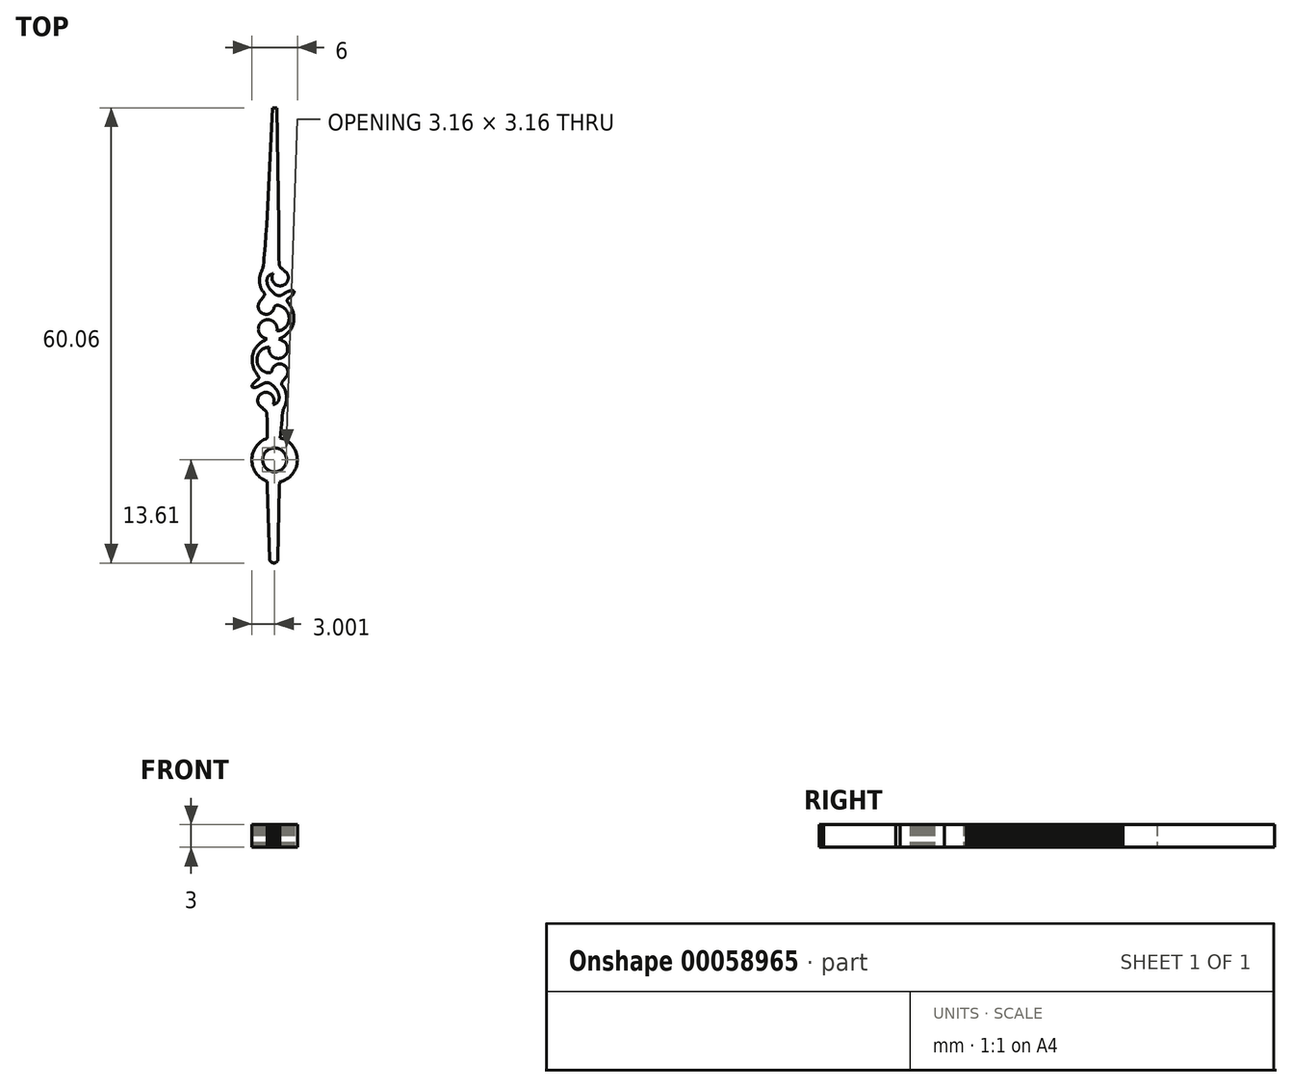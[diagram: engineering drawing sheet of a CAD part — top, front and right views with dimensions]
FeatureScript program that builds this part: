
annotation { "Feature Type Name" : "Feature", "Feature Type Description" : "" }
export const myFeature = defineFeature(function(context is Context, id is Id, definition is map)
    precondition{}
    {
        {
            var Q0;
            Q0=qCreatedBy(makeId("Top.planeOp"),FACE);
            var sketch = newSketch(context, id + "F0", { "sketchPlane" : qUnion([Q0])});
            skLineSegment(sketch, "E0", {"start": v(-0.15, 30.03) * mm, "end": v(0.45, 30.03) * mm});
            skLineSegment(sketch, "E1", {"start": v(0.45, 30.03) * mm, "end": v(0.66, 14.62) * mm});
            skLineSegment(sketch, "E2", {"start": v(0.66, 14.62) * mm, "end": v(0.66, 13.4) * mm});
            skLineSegment(sketch, "E3", {"start": v(0.66, 13.4) * mm, "end": v(0.67, 12.16) * mm});
            skLineSegment(sketch, "E4", {"start": v(0.67, 12.16) * mm, "end": v(0.68, 11.56) * mm});
            skLineSegment(sketch, "E5", {"start": v(0.68, 11.56) * mm, "end": v(0.69, 11) * mm});
            skLineSegment(sketch, "E6", {"start": v(0.69, 11) * mm, "end": v(0.7, 10.49) * mm});
            skLineSegment(sketch, "E7", {"start": v(0.7, 10.49) * mm, "end": v(0.72, 10.03) * mm});
            skLineSegment(sketch, "E8", {"start": v(0.72, 10.03) * mm, "end": v(0.73, 9.66) * mm});
            skLineSegment(sketch, "E9", {"start": v(0.73, 9.66) * mm, "end": v(0.75, 9.37) * mm});
            skLineSegment(sketch, "E10", {"start": v(0.75, 9.37) * mm, "end": v(0.76, 9.3) * mm});
            skLineSegment(sketch, "E11", {"start": v(0.76, 9.3) * mm, "end": v(0.78, 9.23) * mm});
            skLineSegment(sketch, "E12", {"start": v(0.78, 9.23) * mm, "end": v(0.8, 9.16) * mm});
            skLineSegment(sketch, "E13", {"start": v(0.8, 9.16) * mm, "end": v(0.83, 9.1) * mm});
            skLineSegment(sketch, "E14", {"start": v(0.83, 9.1) * mm, "end": v(0.87, 9.05) * mm});
            skLineSegment(sketch, "E15", {"start": v(0.87, 9.05) * mm, "end": v(0.9, 9) * mm});
            skLineSegment(sketch, "E16", {"start": v(0.9, 9) * mm, "end": v(0.94, 8.95) * mm});
            skLineSegment(sketch, "E17", {"start": v(0.94, 8.95) * mm, "end": v(0.98, 8.91) * mm});
            skLineSegment(sketch, "E18", {"start": v(0.98, 8.91) * mm, "end": v(1.07, 8.83) * mm});
            skLineSegment(sketch, "E19", {"start": v(1.07, 8.83) * mm, "end": v(1.16, 8.76) * mm});
            skLineSegment(sketch, "E20", {"start": v(1.16, 8.76) * mm, "end": v(1.25, 8.68) * mm});
            skLineSegment(sketch, "E21", {"start": v(1.25, 8.68) * mm, "end": v(1.29, 8.64) * mm});
            skLineSegment(sketch, "E22", {"start": v(1.29, 8.64) * mm, "end": v(1.32, 8.6) * mm});
            skLineSegment(sketch, "E23", {"start": v(1.32, 8.6) * mm, "end": v(1.32, 8.6) * mm});
            skLineSegment(sketch, "E24", {"start": v(1.32, 8.6) * mm, "end": v(1.46, 8.5) * mm});
            skLineSegment(sketch, "E25", {"start": v(1.46, 8.5) * mm, "end": v(1.52, 8.44) * mm});
            skLineSegment(sketch, "E26", {"start": v(1.52, 8.44) * mm, "end": v(1.58, 8.4) * mm});
            skLineSegment(sketch, "E27", {"start": v(1.58, 8.4) * mm, "end": v(1.64, 8.34) * mm});
            skLineSegment(sketch, "E28", {"start": v(1.64, 8.34) * mm, "end": v(1.69, 8.28) * mm});
            skLineSegment(sketch, "E29", {"start": v(1.69, 8.28) * mm, "end": v(1.74, 8.23) * mm});
            skLineSegment(sketch, "E30", {"start": v(1.74, 8.23) * mm, "end": v(1.78, 8.17) * mm});
            skLineSegment(sketch, "E31", {"start": v(1.78, 8.17) * mm, "end": v(1.82, 8.11) * mm});
            skLineSegment(sketch, "E32", {"start": v(1.82, 8.11) * mm, "end": v(1.85, 8.05) * mm});
            skLineSegment(sketch, "E33", {"start": v(1.85, 8.05) * mm, "end": v(1.88, 7.99) * mm});
            skLineSegment(sketch, "E34", {"start": v(1.88, 7.99) * mm, "end": v(1.9, 7.92) * mm});
            skLineSegment(sketch, "E35", {"start": v(1.9, 7.92) * mm, "end": v(1.92, 7.85) * mm});
            skLineSegment(sketch, "E36", {"start": v(1.92, 7.85) * mm, "end": v(1.94, 7.78) * mm});
            skLineSegment(sketch, "E37", {"start": v(1.94, 7.78) * mm, "end": v(1.94, 7.7) * mm});
            skLineSegment(sketch, "E38", {"start": v(1.94, 7.7) * mm, "end": v(1.95, 7.62) * mm});
            skLineSegment(sketch, "E39", {"start": v(1.95, 7.62) * mm, "end": v(1.94, 7.57) * mm});
            skLineSegment(sketch, "E40", {"start": v(1.94, 7.57) * mm, "end": v(1.94, 7.51) * mm});
            skLineSegment(sketch, "E41", {"start": v(1.94, 7.51) * mm, "end": v(1.93, 7.46) * mm});
            skLineSegment(sketch, "E42", {"start": v(1.93, 7.46) * mm, "end": v(1.92, 7.4) * mm});
            skLineSegment(sketch, "E43", {"start": v(1.92, 7.4) * mm, "end": v(1.91, 7.35) * mm});
            skLineSegment(sketch, "E44", {"start": v(1.91, 7.35) * mm, "end": v(1.9, 7.3) * mm});
            skLineSegment(sketch, "E45", {"start": v(1.9, 7.3) * mm, "end": v(1.88, 7.25) * mm});
            skLineSegment(sketch, "E46", {"start": v(1.88, 7.25) * mm, "end": v(1.86, 7.2) * mm});
            skLineSegment(sketch, "E47", {"start": v(1.86, 7.2) * mm, "end": v(1.84, 7.16) * mm});
            skLineSegment(sketch, "E48", {"start": v(1.84, 7.16) * mm, "end": v(1.82, 7.1) * mm});
            skLineSegment(sketch, "E49", {"start": v(1.82, 7.1) * mm, "end": v(1.76, 7.02) * mm});
            skLineSegment(sketch, "E50", {"start": v(1.76, 7.02) * mm, "end": v(1.7, 6.94) * mm});
            skLineSegment(sketch, "E51", {"start": v(1.7, 6.94) * mm, "end": v(1.63, 6.86) * mm});
            skLineSegment(sketch, "E52", {"start": v(1.63, 6.86) * mm, "end": v(1.55, 6.79) * mm});
            skLineSegment(sketch, "E53", {"start": v(1.55, 6.79) * mm, "end": v(1.47, 6.73) * mm});
            skLineSegment(sketch, "E54", {"start": v(1.47, 6.73) * mm, "end": v(1.38, 6.67) * mm});
            skLineSegment(sketch, "E55", {"start": v(1.38, 6.67) * mm, "end": v(1.33, 6.65) * mm});
            skLineSegment(sketch, "E56", {"start": v(1.33, 6.65) * mm, "end": v(1.29, 6.63) * mm});
            skLineSegment(sketch, "E57", {"start": v(1.29, 6.63) * mm, "end": v(1.24, 6.6) * mm});
            skLineSegment(sketch, "E58", {"start": v(1.24, 6.6) * mm, "end": v(1.19, 6.6) * mm});
            skLineSegment(sketch, "E59", {"start": v(1.19, 6.6) * mm, "end": v(1.13, 6.58) * mm});
            skLineSegment(sketch, "E60", {"start": v(1.13, 6.58) * mm, "end": v(1.08, 6.56) * mm});
            skLineSegment(sketch, "E61", {"start": v(1.08, 6.56) * mm, "end": v(1.03, 6.56) * mm});
            skLineSegment(sketch, "E62", {"start": v(1.03, 6.56) * mm, "end": v(0.97, 6.55) * mm});
            skLineSegment(sketch, "E63", {"start": v(0.97, 6.55) * mm, "end": v(0.92, 6.54) * mm});
            skLineSegment(sketch, "E64", {"start": v(0.92, 6.54) * mm, "end": v(0.86, 6.54) * mm});
            skLineSegment(sketch, "E65", {"start": v(0.86, 6.54) * mm, "end": v(0.8, 6.54) * mm});
            skLineSegment(sketch, "E66", {"start": v(0.8, 6.54) * mm, "end": v(0.75, 6.55) * mm});
            skLineSegment(sketch, "E67", {"start": v(0.75, 6.55) * mm, "end": v(0.7, 6.56) * mm});
            skLineSegment(sketch, "E68", {"start": v(0.7, 6.56) * mm, "end": v(0.65, 6.56) * mm});
            skLineSegment(sketch, "E69", {"start": v(0.65, 6.56) * mm, "end": v(0.6, 6.58) * mm});
            skLineSegment(sketch, "E70", {"start": v(0.6, 6.58) * mm, "end": v(0.54, 6.6) * mm});
            skLineSegment(sketch, "E71", {"start": v(0.54, 6.6) * mm, "end": v(0.5, 6.6) * mm});
            skLineSegment(sketch, "E72", {"start": v(0.5, 6.6) * mm, "end": v(0.44, 6.63) * mm});
            skLineSegment(sketch, "E73", {"start": v(0.44, 6.63) * mm, "end": v(0.4, 6.65) * mm});
            skLineSegment(sketch, "E74", {"start": v(0.4, 6.65) * mm, "end": v(0.35, 6.67) * mm});
            skLineSegment(sketch, "E75", {"start": v(0.35, 6.67) * mm, "end": v(0.26, 6.73) * mm});
            skLineSegment(sketch, "E76", {"start": v(0.26, 6.73) * mm, "end": v(0.18, 6.79) * mm});
            skLineSegment(sketch, "E77", {"start": v(0.18, 6.79) * mm, "end": v(0.1, 6.86) * mm});
            skLineSegment(sketch, "E78", {"start": v(0.1, 6.86) * mm, "end": v(0.03, 6.94) * mm});
            skLineSegment(sketch, "E79", {"start": v(0.03, 6.94) * mm, "end": v(-0.03, 7.02) * mm});
            skLineSegment(sketch, "E80", {"start": v(-0.03, 7.02) * mm, "end": v(-0.09, 7.1) * mm});
            skLineSegment(sketch, "E81", {"start": v(-0.09, 7.1) * mm, "end": v(-0.11, 7.16) * mm});
            skLineSegment(sketch, "E82", {"start": v(-0.11, 7.16) * mm, "end": v(-0.13, 7.2) * mm});
            skLineSegment(sketch, "E83", {"start": v(-0.13, 7.2) * mm, "end": v(-0.15, 7.25) * mm});
            skLineSegment(sketch, "E84", {"start": v(-0.15, 7.25) * mm, "end": v(-0.17, 7.3) * mm});
            skLineSegment(sketch, "E85", {"start": v(-0.17, 7.3) * mm, "end": v(-0.18, 7.35) * mm});
            skLineSegment(sketch, "E86", {"start": v(-0.18, 7.35) * mm, "end": v(-0.2, 7.4) * mm});
            skLineSegment(sketch, "E87", {"start": v(-0.2, 7.4) * mm, "end": v(-0.2, 7.46) * mm});
            skLineSegment(sketch, "E88", {"start": v(-0.2, 7.46) * mm, "end": v(-0.21, 7.51) * mm});
            skLineSegment(sketch, "E89", {"start": v(-0.21, 7.51) * mm, "end": v(-0.22, 7.57) * mm});
            skLineSegment(sketch, "E90", {"start": v(-0.22, 7.57) * mm, "end": v(-0.22, 7.62) * mm});
            skLineSegment(sketch, "E91", {"start": v(-0.22, 7.62) * mm, "end": v(-0.22, 7.7) * mm});
            skLineSegment(sketch, "E92", {"start": v(-0.22, 7.7) * mm, "end": v(-0.2, 7.77) * mm});
            skLineSegment(sketch, "E93", {"start": v(-0.2, 7.77) * mm, "end": v(-0.2, 7.84) * mm});
            skLineSegment(sketch, "E94", {"start": v(-0.2, 7.84) * mm, "end": v(-0.18, 7.9) * mm});
            skLineSegment(sketch, "E95", {"start": v(-0.18, 7.9) * mm, "end": v(-0.16, 7.97) * mm});
            skLineSegment(sketch, "E96", {"start": v(-0.16, 7.97) * mm, "end": v(-0.14, 8.04) * mm});
            skLineSegment(sketch, "E97", {"start": v(-0.14, 8.04) * mm, "end": v(-0.1, 8.1) * mm});
            skLineSegment(sketch, "E98", {"start": v(-0.1, 8.1) * mm, "end": v(-0.08, 8.16) * mm});
            skLineSegment(sketch, "E99", {"start": v(-0.08, 8.16) * mm, "end": v(-0.1, 8.16) * mm});
            skLineSegment(sketch, "E100", {"start": v(-0.1, 8.16) * mm, "end": v(-0.14, 8.15) * mm});
            skLineSegment(sketch, "E101", {"start": v(-0.14, 8.15) * mm, "end": v(-0.23, 8.11) * mm});
            skLineSegment(sketch, "E102", {"start": v(-0.23, 8.11) * mm, "end": v(-0.34, 8.06) * mm});
            skLineSegment(sketch, "E103", {"start": v(-0.34, 8.06) * mm, "end": v(-0.48, 8) * mm});
            skLineSegment(sketch, "E104", {"start": v(-0.48, 8) * mm, "end": v(-0.53, 7.97) * mm});
            skLineSegment(sketch, "E105", {"start": v(-0.53, 7.97) * mm, "end": v(-0.58, 7.94) * mm});
            skLineSegment(sketch, "E106", {"start": v(-0.58, 7.94) * mm, "end": v(-0.62, 7.9) * mm});
            skLineSegment(sketch, "E107", {"start": v(-0.62, 7.9) * mm, "end": v(-0.66, 7.86) * mm});
            skLineSegment(sketch, "E108", {"start": v(-0.66, 7.86) * mm, "end": v(-0.7, 7.82) * mm});
            skLineSegment(sketch, "E109", {"start": v(-0.7, 7.82) * mm, "end": v(-0.74, 7.77) * mm});
            skLineSegment(sketch, "E110", {"start": v(-0.74, 7.77) * mm, "end": v(-0.77, 7.72) * mm});
            skLineSegment(sketch, "E111", {"start": v(-0.77, 7.72) * mm, "end": v(-0.8, 7.67) * mm});
            skLineSegment(sketch, "E112", {"start": v(-0.8, 7.67) * mm, "end": v(-0.82, 7.62) * mm});
            skLineSegment(sketch, "E113", {"start": v(-0.82, 7.62) * mm, "end": v(-0.84, 7.56) * mm});
            skLineSegment(sketch, "E114", {"start": v(-0.84, 7.56) * mm, "end": v(-0.85, 7.5) * mm});
            skLineSegment(sketch, "E115", {"start": v(-0.85, 7.5) * mm, "end": v(-0.87, 7.44) * mm});
            skLineSegment(sketch, "E116", {"start": v(-0.87, 7.44) * mm, "end": v(-0.88, 7.38) * mm});
            skLineSegment(sketch, "E117", {"start": v(-0.88, 7.38) * mm, "end": v(-0.88, 7.31) * mm});
            skLineSegment(sketch, "E118", {"start": v(-0.88, 7.31) * mm, "end": v(-0.88, 7.25) * mm});
            skLineSegment(sketch, "E119", {"start": v(-0.88, 7.25) * mm, "end": v(-0.88, 7.18) * mm});
            skLineSegment(sketch, "E120", {"start": v(-0.88, 7.18) * mm, "end": v(-0.88, 7.1) * mm});
            skLineSegment(sketch, "E121", {"start": v(-0.88, 7.1) * mm, "end": v(-0.87, 7.04) * mm});
            skLineSegment(sketch, "E122", {"start": v(-0.87, 7.04) * mm, "end": v(-0.86, 6.97) * mm});
            skLineSegment(sketch, "E123", {"start": v(-0.86, 6.97) * mm, "end": v(-0.84, 6.9) * mm});
            skLineSegment(sketch, "E124", {"start": v(-0.84, 6.9) * mm, "end": v(-0.83, 6.82) * mm});
            skLineSegment(sketch, "E125", {"start": v(-0.83, 6.82) * mm, "end": v(-0.8, 6.75) * mm});
            skLineSegment(sketch, "E126", {"start": v(-0.8, 6.75) * mm, "end": v(-0.78, 6.68) * mm});
            skLineSegment(sketch, "E127", {"start": v(-0.78, 6.68) * mm, "end": v(-0.75, 6.6) * mm});
            skLineSegment(sketch, "E128", {"start": v(-0.75, 6.6) * mm, "end": v(-0.72, 6.53) * mm});
            skLineSegment(sketch, "E129", {"start": v(-0.72, 6.53) * mm, "end": v(-0.68, 6.45) * mm});
            skLineSegment(sketch, "E130", {"start": v(-0.68, 6.45) * mm, "end": v(-0.64, 6.38) * mm});
            skLineSegment(sketch, "E131", {"start": v(-0.64, 6.38) * mm, "end": v(-0.6, 6.3) * mm});
            skLineSegment(sketch, "E132", {"start": v(-0.6, 6.3) * mm, "end": v(-0.56, 6.23) * mm});
            skLineSegment(sketch, "E133", {"start": v(-0.56, 6.23) * mm, "end": v(-0.5, 6.16) * mm});
            skLineSegment(sketch, "E134", {"start": v(-0.5, 6.16) * mm, "end": v(-0.45, 6.09) * mm});
            skLineSegment(sketch, "E135", {"start": v(-0.45, 6.09) * mm, "end": v(-0.4, 6.02) * mm});
            skLineSegment(sketch, "E136", {"start": v(-0.4, 6.02) * mm, "end": v(-0.27, 5.87) * mm});
            skLineSegment(sketch, "E137", {"start": v(-0.27, 5.87) * mm, "end": v(-0.15, 5.73) * mm});
            skLineSegment(sketch, "E138", {"start": v(-0.15, 5.73) * mm, "end": v(-0.03, 5.62) * mm});
            skLineSegment(sketch, "E139", {"start": v(-0.03, 5.62) * mm, "end": v(0.03, 5.57) * mm});
            skLineSegment(sketch, "E140", {"start": v(0.03, 5.57) * mm, "end": v(0.08, 5.52) * mm});
            skLineSegment(sketch, "E141", {"start": v(0.08, 5.52) * mm, "end": v(0.14, 5.47) * mm});
            skLineSegment(sketch, "E142", {"start": v(0.14, 5.47) * mm, "end": v(0.2, 5.43) * mm});
            skLineSegment(sketch, "E143", {"start": v(0.2, 5.43) * mm, "end": v(0.25, 5.4) * mm});
            skLineSegment(sketch, "E144", {"start": v(0.25, 5.4) * mm, "end": v(0.3, 5.37) * mm});
            skLineSegment(sketch, "E145", {"start": v(0.3, 5.37) * mm, "end": v(0.36, 5.34) * mm});
            skLineSegment(sketch, "E146", {"start": v(0.36, 5.34) * mm, "end": v(0.42, 5.32) * mm});
            skLineSegment(sketch, "E147", {"start": v(0.42, 5.32) * mm, "end": v(0.47, 5.3) * mm});
            skLineSegment(sketch, "E148", {"start": v(0.47, 5.3) * mm, "end": v(0.53, 5.28) * mm});
            skLineSegment(sketch, "E149", {"start": v(0.53, 5.28) * mm, "end": v(0.58, 5.27) * mm});
            skLineSegment(sketch, "E150", {"start": v(0.58, 5.27) * mm, "end": v(0.64, 5.26) * mm});
            skLineSegment(sketch, "E151", {"start": v(0.64, 5.26) * mm, "end": v(0.7, 5.26) * mm});
            skLineSegment(sketch, "E152", {"start": v(0.7, 5.26) * mm, "end": v(0.75, 5.26) * mm});
            skLineSegment(sketch, "E153", {"start": v(0.75, 5.26) * mm, "end": v(0.8, 5.26) * mm});
            skLineSegment(sketch, "E154", {"start": v(0.8, 5.26) * mm, "end": v(0.86, 5.27) * mm});
            skLineSegment(sketch, "E155", {"start": v(0.86, 5.27) * mm, "end": v(0.92, 5.28) * mm});
            skLineSegment(sketch, "E156", {"start": v(0.92, 5.28) * mm, "end": v(0.98, 5.3) * mm});
            skLineSegment(sketch, "E157", {"start": v(0.98, 5.3) * mm, "end": v(1.04, 5.31) * mm});
            skLineSegment(sketch, "E158", {"start": v(1.04, 5.31) * mm, "end": v(1.1, 5.33) * mm});
            skLineSegment(sketch, "E159", {"start": v(1.1, 5.33) * mm, "end": v(1.16, 5.36) * mm});
            skLineSegment(sketch, "E160", {"start": v(1.16, 5.36) * mm, "end": v(1.22, 5.4) * mm});
            skLineSegment(sketch, "E161", {"start": v(1.22, 5.4) * mm, "end": v(1.28, 5.42) * mm});
            skLineSegment(sketch, "E162", {"start": v(1.28, 5.42) * mm, "end": v(1.34, 5.46) * mm});
            skLineSegment(sketch, "E163", {"start": v(1.34, 5.46) * mm, "end": v(1.47, 5.55) * mm});
            skLineSegment(sketch, "E164", {"start": v(1.47, 5.55) * mm, "end": v(1.58, 5.61) * mm});
            skLineSegment(sketch, "E165", {"start": v(1.58, 5.61) * mm, "end": v(1.67, 5.67) * mm});
            skLineSegment(sketch, "E166", {"start": v(1.67, 5.67) * mm, "end": v(1.77, 5.73) * mm});
            skLineSegment(sketch, "E167", {"start": v(1.77, 5.73) * mm, "end": v(1.86, 5.77) * mm});
            skLineSegment(sketch, "E168", {"start": v(1.86, 5.77) * mm, "end": v(1.95, 5.81) * mm});
            skLineSegment(sketch, "E169", {"start": v(1.95, 5.81) * mm, "end": v(2.03, 5.85) * mm});
            skLineSegment(sketch, "E170", {"start": v(2.03, 5.85) * mm, "end": v(2.11, 5.88) * mm});
            skLineSegment(sketch, "E171", {"start": v(2.11, 5.88) * mm, "end": v(2.2, 5.9) * mm});
            skLineSegment(sketch, "E172", {"start": v(2.2, 5.9) * mm, "end": v(2.26, 5.92) * mm});
            skLineSegment(sketch, "E173", {"start": v(2.26, 5.92) * mm, "end": v(2.33, 5.93) * mm});
            skLineSegment(sketch, "E174", {"start": v(2.33, 5.93) * mm, "end": v(2.4, 5.93) * mm});
            skLineSegment(sketch, "E175", {"start": v(2.4, 5.93) * mm, "end": v(2.45, 5.93) * mm});
            skLineSegment(sketch, "E176", {"start": v(2.45, 5.93) * mm, "end": v(2.5, 5.93) * mm});
            skLineSegment(sketch, "E177", {"start": v(2.5, 5.93) * mm, "end": v(2.55, 5.92) * mm});
            skLineSegment(sketch, "E178", {"start": v(2.55, 5.92) * mm, "end": v(2.59, 5.9) * mm});
            skLineSegment(sketch, "E179", {"start": v(2.59, 5.9) * mm, "end": v(2.62, 5.88) * mm});
            skLineSegment(sketch, "E180", {"start": v(2.62, 5.88) * mm, "end": v(2.65, 5.86) * mm});
            skLineSegment(sketch, "E181", {"start": v(2.65, 5.86) * mm, "end": v(2.67, 5.83) * mm});
            skLineSegment(sketch, "E182", {"start": v(2.67, 5.83) * mm, "end": v(2.69, 5.8) * mm});
            skLineSegment(sketch, "E183", {"start": v(2.69, 5.8) * mm, "end": v(2.7, 5.76) * mm});
            skLineSegment(sketch, "E184", {"start": v(2.7, 5.76) * mm, "end": v(2.7, 5.72) * mm});
            skLineSegment(sketch, "E185", {"start": v(2.7, 5.72) * mm, "end": v(2.7, 5.67) * mm});
            skLineSegment(sketch, "E186", {"start": v(2.7, 5.67) * mm, "end": v(2.68, 5.63) * mm});
            skLineSegment(sketch, "E187", {"start": v(2.68, 5.63) * mm, "end": v(2.66, 5.57) * mm});
            skLineSegment(sketch, "E188", {"start": v(2.66, 5.57) * mm, "end": v(2.63, 5.52) * mm});
            skLineSegment(sketch, "E189", {"start": v(2.63, 5.52) * mm, "end": v(2.6, 5.46) * mm});
            skLineSegment(sketch, "E190", {"start": v(2.6, 5.46) * mm, "end": v(2.54, 5.4) * mm});
            skLineSegment(sketch, "E191", {"start": v(2.54, 5.4) * mm, "end": v(2.5, 5.34) * mm});
            skLineSegment(sketch, "E192", {"start": v(2.5, 5.34) * mm, "end": v(2.43, 5.27) * mm});
            skLineSegment(sketch, "E193", {"start": v(2.43, 5.27) * mm, "end": v(2.35, 5.2) * mm});
            skLineSegment(sketch, "E194", {"start": v(2.35, 5.2) * mm, "end": v(2.27, 5.13) * mm});
            skLineSegment(sketch, "E195", {"start": v(2.27, 5.13) * mm, "end": v(2.18, 5.05) * mm});
            skLineSegment(sketch, "E196", {"start": v(2.18, 5.05) * mm, "end": v(2, 4.92) * mm});
            skLineSegment(sketch, "E197", {"start": v(2, 4.92) * mm, "end": v(1.94, 4.86) * mm});
            skLineSegment(sketch, "E198", {"start": v(1.94, 4.86) * mm, "end": v(1.89, 4.81) * mm});
            skLineSegment(sketch, "E199", {"start": v(1.89, 4.81) * mm, "end": v(1.85, 4.76) * mm});
            skLineSegment(sketch, "E200", {"start": v(1.85, 4.76) * mm, "end": v(1.81, 4.71) * mm});
            skLineSegment(sketch, "E201", {"start": v(1.81, 4.71) * mm, "end": v(1.8, 4.69) * mm});
            skLineSegment(sketch, "E202", {"start": v(1.8, 4.69) * mm, "end": v(1.8, 4.67) * mm});
            skLineSegment(sketch, "E203", {"start": v(1.8, 4.67) * mm, "end": v(1.8, 4.64) * mm});
            skLineSegment(sketch, "E204", {"start": v(1.8, 4.64) * mm, "end": v(1.79, 4.62) * mm});
            skLineSegment(sketch, "E205", {"start": v(1.79, 4.62) * mm, "end": v(1.8, 4.59) * mm});
            skLineSegment(sketch, "E206", {"start": v(1.8, 4.59) * mm, "end": v(1.8, 4.56) * mm});
            skLineSegment(sketch, "E207", {"start": v(1.8, 4.56) * mm, "end": v(1.81, 4.5) * mm});
            skLineSegment(sketch, "E208", {"start": v(1.81, 4.5) * mm, "end": v(1.84, 4.44) * mm});
            skLineSegment(sketch, "E209", {"start": v(1.84, 4.44) * mm, "end": v(1.88, 4.36) * mm});
            skLineSegment(sketch, "E210", {"start": v(1.88, 4.36) * mm, "end": v(1.93, 4.28) * mm});
            skLineSegment(sketch, "E211", {"start": v(1.93, 4.28) * mm, "end": v(2, 4.18) * mm});
            skLineSegment(sketch, "E212", {"start": v(2, 4.18) * mm, "end": v(2.16, 3.95) * mm});
            skLineSegment(sketch, "E213", {"start": v(2.16, 3.95) * mm, "end": v(2.23, 3.86) * mm});
            skLineSegment(sketch, "E214", {"start": v(2.23, 3.86) * mm, "end": v(2.29, 3.76) * mm});
            skLineSegment(sketch, "E215", {"start": v(2.29, 3.76) * mm, "end": v(2.34, 3.66) * mm});
            skLineSegment(sketch, "E216", {"start": v(2.34, 3.66) * mm, "end": v(2.4, 3.56) * mm});
            skLineSegment(sketch, "E217", {"start": v(2.4, 3.56) * mm, "end": v(2.44, 3.45) * mm});
            skLineSegment(sketch, "E218", {"start": v(2.44, 3.45) * mm, "end": v(2.49, 3.34) * mm});
            skLineSegment(sketch, "E219", {"start": v(2.49, 3.34) * mm, "end": v(2.53, 3.23) * mm});
            skLineSegment(sketch, "E220", {"start": v(2.53, 3.23) * mm, "end": v(2.56, 3.12) * mm});
            skLineSegment(sketch, "E221", {"start": v(2.56, 3.12) * mm, "end": v(2.59, 3) * mm});
            skLineSegment(sketch, "E222", {"start": v(2.59, 3) * mm, "end": v(2.62, 2.9) * mm});
            skLineSegment(sketch, "E223", {"start": v(2.62, 2.9) * mm, "end": v(2.64, 2.78) * mm});
            skLineSegment(sketch, "E224", {"start": v(2.64, 2.78) * mm, "end": v(2.65, 2.66) * mm});
            skLineSegment(sketch, "E225", {"start": v(2.65, 2.66) * mm, "end": v(2.67, 2.55) * mm});
            skLineSegment(sketch, "E226", {"start": v(2.67, 2.55) * mm, "end": v(2.68, 2.43) * mm});
            skLineSegment(sketch, "E227", {"start": v(2.68, 2.43) * mm, "end": v(2.68, 2.31) * mm});
            skLineSegment(sketch, "E228", {"start": v(2.68, 2.31) * mm, "end": v(2.68, 2.2) * mm});
            skLineSegment(sketch, "E229", {"start": v(2.68, 2.2) * mm, "end": v(2.67, 2.08) * mm});
            skLineSegment(sketch, "E230", {"start": v(2.67, 2.08) * mm, "end": v(2.67, 1.96) * mm});
            skLineSegment(sketch, "E231", {"start": v(2.67, 1.96) * mm, "end": v(2.65, 1.85) * mm});
            skLineSegment(sketch, "E232", {"start": v(2.65, 1.85) * mm, "end": v(2.64, 1.74) * mm});
            skLineSegment(sketch, "E233", {"start": v(2.64, 1.74) * mm, "end": v(2.61, 1.62) * mm});
            skLineSegment(sketch, "E234", {"start": v(2.61, 1.62) * mm, "end": v(2.59, 1.51) * mm});
            skLineSegment(sketch, "E235", {"start": v(2.59, 1.51) * mm, "end": v(2.56, 1.4) * mm});
            skLineSegment(sketch, "E236", {"start": v(2.56, 1.4) * mm, "end": v(2.52, 1.3) * mm});
            skLineSegment(sketch, "E237", {"start": v(2.52, 1.3) * mm, "end": v(2.49, 1.2) * mm});
            skLineSegment(sketch, "E238", {"start": v(2.49, 1.2) * mm, "end": v(2.44, 1.09) * mm});
            skLineSegment(sketch, "E239", {"start": v(2.44, 1.09) * mm, "end": v(2.4, 0.99) * mm});
            skLineSegment(sketch, "E240", {"start": v(2.4, 0.99) * mm, "end": v(2.34, 0.9) * mm});
            skLineSegment(sketch, "E241", {"start": v(2.34, 0.9) * mm, "end": v(2.29, 0.8) * mm});
            skLineSegment(sketch, "E242", {"start": v(2.29, 0.8) * mm, "end": v(2.23, 0.7) * mm});
            skLineSegment(sketch, "E243", {"start": v(2.23, 0.7) * mm, "end": v(2.16, 0.62) * mm});
            skLineSegment(sketch, "E244", {"start": v(2.16, 0.62) * mm, "end": v(2.1, 0.54) * mm});
            skLineSegment(sketch, "E245", {"start": v(2.1, 0.54) * mm, "end": v(1.97, 0.4) * mm});
            skLineSegment(sketch, "E246", {"start": v(1.97, 0.4) * mm, "end": v(1.84, 0.27) * mm});
            skLineSegment(sketch, "E247", {"start": v(1.84, 0.27) * mm, "end": v(1.71, 0.15) * mm});
            skLineSegment(sketch, "E248", {"start": v(1.71, 0.15) * mm, "end": v(1.58, 0.03) * mm});
            skLineSegment(sketch, "E249", {"start": v(1.58, 0.03) * mm, "end": v(1.44, -0.07) * mm});
            skLineSegment(sketch, "E250", {"start": v(1.44, -0.07) * mm, "end": v(1.3, -0.17) * mm});
            skLineSegment(sketch, "E251", {"start": v(1.3, -0.17) * mm, "end": v(1.15, -0.26) * mm});
            skLineSegment(sketch, "E252", {"start": v(1.15, -0.26) * mm, "end": v(1.01, -0.34) * mm});
            skLineSegment(sketch, "E253", {"start": v(1.01, -0.34) * mm, "end": v(0.87, -0.41) * mm});
            skLineSegment(sketch, "E254", {"start": v(0.87, -0.41) * mm, "end": v(0.72, -0.47) * mm});
            skLineSegment(sketch, "E255", {"start": v(0.72, -0.47) * mm, "end": v(0.7, -0.48) * mm});
            skLineSegment(sketch, "E256", {"start": v(0.7, -0.48) * mm, "end": v(0.78, -0.5) * mm});
            skLineSegment(sketch, "E257", {"start": v(0.78, -0.5) * mm, "end": v(0.9, -0.56) * mm});
            skLineSegment(sketch, "E258", {"start": v(0.9, -0.56) * mm, "end": v(1.08, -0.64) * mm});
            skLineSegment(sketch, "E259", {"start": v(1.08, -0.64) * mm, "end": v(1.2, -0.7) * mm});
            skLineSegment(sketch, "E260", {"start": v(1.2, -0.7) * mm, "end": v(1.26, -0.73) * mm});
            skLineSegment(sketch, "E261", {"start": v(1.26, -0.73) * mm, "end": v(1.33, -0.77) * mm});
            skLineSegment(sketch, "E262", {"start": v(1.33, -0.77) * mm, "end": v(1.39, -0.82) * mm});
            skLineSegment(sketch, "E263", {"start": v(1.39, -0.82) * mm, "end": v(1.45, -0.87) * mm});
            skLineSegment(sketch, "E264", {"start": v(1.45, -0.87) * mm, "end": v(1.5, -0.93) * mm});
            skLineSegment(sketch, "E265", {"start": v(1.5, -0.93) * mm, "end": v(1.56, -0.98) * mm});
            skLineSegment(sketch, "E266", {"start": v(1.56, -0.98) * mm, "end": v(1.6, -1.05) * mm});
            skLineSegment(sketch, "E267", {"start": v(1.6, -1.05) * mm, "end": v(1.65, -1.1) * mm});
            skLineSegment(sketch, "E268", {"start": v(1.65, -1.1) * mm, "end": v(1.7, -1.18) * mm});
            skLineSegment(sketch, "E269", {"start": v(1.7, -1.18) * mm, "end": v(1.73, -1.25) * mm});
            skLineSegment(sketch, "E270", {"start": v(1.73, -1.25) * mm, "end": v(1.77, -1.32) * mm});
            skLineSegment(sketch, "E271", {"start": v(1.77, -1.32) * mm, "end": v(1.8, -1.4) * mm});
            skLineSegment(sketch, "E272", {"start": v(1.8, -1.4) * mm, "end": v(1.82, -1.47) * mm});
            skLineSegment(sketch, "E273", {"start": v(1.82, -1.47) * mm, "end": v(1.84, -1.55) * mm});
            skLineSegment(sketch, "E274", {"start": v(1.84, -1.55) * mm, "end": v(1.85, -1.63) * mm});
            skLineSegment(sketch, "E275", {"start": v(1.85, -1.63) * mm, "end": v(1.86, -1.71) * mm});
            skLineSegment(sketch, "E276", {"start": v(1.86, -1.71) * mm, "end": v(1.86, -1.8) * mm});
            skLineSegment(sketch, "E277", {"start": v(1.86, -1.8) * mm, "end": v(1.86, -1.86) * mm});
            skLineSegment(sketch, "E278", {"start": v(1.86, -1.86) * mm, "end": v(1.86, -1.92) * mm});
            skLineSegment(sketch, "E279", {"start": v(1.86, -1.92) * mm, "end": v(1.85, -1.99) * mm});
            skLineSegment(sketch, "E280", {"start": v(1.85, -1.99) * mm, "end": v(1.84, -2.05) * mm});
            skLineSegment(sketch, "E281", {"start": v(1.84, -2.05) * mm, "end": v(1.82, -2.1) * mm});
            skLineSegment(sketch, "E282", {"start": v(1.82, -2.1) * mm, "end": v(1.8, -2.17) * mm});
            skLineSegment(sketch, "E283", {"start": v(1.8, -2.17) * mm, "end": v(1.79, -2.22) * mm});
            skLineSegment(sketch, "E284", {"start": v(1.79, -2.22) * mm, "end": v(1.76, -2.28) * mm});
            skLineSegment(sketch, "E285", {"start": v(1.76, -2.28) * mm, "end": v(1.74, -2.34) * mm});
            skLineSegment(sketch, "E286", {"start": v(1.74, -2.34) * mm, "end": v(1.71, -2.39) * mm});
            skLineSegment(sketch, "E287", {"start": v(1.71, -2.39) * mm, "end": v(1.68, -2.44) * mm});
            skLineSegment(sketch, "E288", {"start": v(1.68, -2.44) * mm, "end": v(1.65, -2.5) * mm});
            skLineSegment(sketch, "E289", {"start": v(1.65, -2.5) * mm, "end": v(1.62, -2.54) * mm});
            skLineSegment(sketch, "E290", {"start": v(1.62, -2.54) * mm, "end": v(1.58, -2.59) * mm});
            skLineSegment(sketch, "E291", {"start": v(1.58, -2.59) * mm, "end": v(1.54, -2.63) * mm});
            skLineSegment(sketch, "E292", {"start": v(1.54, -2.63) * mm, "end": v(1.5, -2.68) * mm});
            skLineSegment(sketch, "E293", {"start": v(1.5, -2.68) * mm, "end": v(1.46, -2.72) * mm});
            skLineSegment(sketch, "E294", {"start": v(1.46, -2.72) * mm, "end": v(1.41, -2.76) * mm});
            skLineSegment(sketch, "E295", {"start": v(1.41, -2.76) * mm, "end": v(1.36, -2.8) * mm});
            skLineSegment(sketch, "E296", {"start": v(1.36, -2.8) * mm, "end": v(1.31, -2.83) * mm});
            skLineSegment(sketch, "E297", {"start": v(1.31, -2.83) * mm, "end": v(1.26, -2.86) * mm});
            skLineSegment(sketch, "E298", {"start": v(1.26, -2.86) * mm, "end": v(1.21, -2.89) * mm});
            skLineSegment(sketch, "E299", {"start": v(1.21, -2.89) * mm, "end": v(1.16, -2.92) * mm});
            skLineSegment(sketch, "E300", {"start": v(1.16, -2.92) * mm, "end": v(1.1, -2.94) * mm});
            skLineSegment(sketch, "E301", {"start": v(1.1, -2.94) * mm, "end": v(1.05, -2.96) * mm});
            skLineSegment(sketch, "E302", {"start": v(1.05, -2.96) * mm, "end": v(0.99, -2.98) * mm});
            skLineSegment(sketch, "E303", {"start": v(0.99, -2.98) * mm, "end": v(0.93, -3) * mm});
            skLineSegment(sketch, "E304", {"start": v(0.93, -3) * mm, "end": v(0.87, -3.01) * mm});
            skLineSegment(sketch, "E305", {"start": v(0.87, -3.01) * mm, "end": v(0.8, -3.02) * mm});
            skLineSegment(sketch, "E306", {"start": v(0.8, -3.02) * mm, "end": v(0.75, -3.03) * mm});
            skLineSegment(sketch, "E307", {"start": v(0.75, -3.03) * mm, "end": v(0.68, -3.04) * mm});
            skLineSegment(sketch, "E308", {"start": v(0.68, -3.04) * mm, "end": v(0.62, -3.04) * mm});
            skLineSegment(sketch, "E309", {"start": v(0.62, -3.04) * mm, "end": v(0.56, -3.04) * mm});
            skLineSegment(sketch, "E310", {"start": v(0.56, -3.04) * mm, "end": v(0.5, -3.03) * mm});
            skLineSegment(sketch, "E311", {"start": v(0.5, -3.03) * mm, "end": v(0.43, -3.02) * mm});
            skLineSegment(sketch, "E312", {"start": v(0.43, -3.02) * mm, "end": v(0.37, -3.01) * mm});
            skLineSegment(sketch, "E313", {"start": v(0.37, -3.01) * mm, "end": v(0.31, -3) * mm});
            skLineSegment(sketch, "E314", {"start": v(0.31, -3) * mm, "end": v(0.25, -2.98) * mm});
            skLineSegment(sketch, "E315", {"start": v(0.25, -2.98) * mm, "end": v(0.2, -2.96) * mm});
            skLineSegment(sketch, "E316", {"start": v(0.2, -2.96) * mm, "end": v(0.14, -2.94) * mm});
            skLineSegment(sketch, "E317", {"start": v(0.14, -2.94) * mm, "end": v(0.08, -2.92) * mm});
            skLineSegment(sketch, "E318", {"start": v(0.08, -2.92) * mm, "end": v(0.03, -2.89) * mm});
            skLineSegment(sketch, "E319", {"start": v(0.03, -2.89) * mm, "end": v(-0.02, -2.86) * mm});
            skLineSegment(sketch, "E320", {"start": v(-0.02, -2.86) * mm, "end": v(-0.07, -2.83) * mm});
            skLineSegment(sketch, "E321", {"start": v(-0.07, -2.83) * mm, "end": v(-0.12, -2.8) * mm});
            skLineSegment(sketch, "E322", {"start": v(-0.12, -2.8) * mm, "end": v(-0.17, -2.76) * mm});
            skLineSegment(sketch, "E323", {"start": v(-0.17, -2.76) * mm, "end": v(-0.21, -2.72) * mm});
            skLineSegment(sketch, "E324", {"start": v(-0.21, -2.72) * mm, "end": v(-0.26, -2.68) * mm});
            skLineSegment(sketch, "E325", {"start": v(-0.26, -2.68) * mm, "end": v(-0.3, -2.63) * mm});
            skLineSegment(sketch, "E326", {"start": v(-0.3, -2.63) * mm, "end": v(-0.34, -2.59) * mm});
            skLineSegment(sketch, "E327", {"start": v(-0.34, -2.59) * mm, "end": v(-0.37, -2.54) * mm});
            skLineSegment(sketch, "E328", {"start": v(-0.37, -2.54) * mm, "end": v(-0.4, -2.5) * mm});
            skLineSegment(sketch, "E329", {"start": v(-0.4, -2.5) * mm, "end": v(-0.44, -2.44) * mm});
            skLineSegment(sketch, "E330", {"start": v(-0.44, -2.44) * mm, "end": v(-0.47, -2.39) * mm});
            skLineSegment(sketch, "E331", {"start": v(-0.47, -2.39) * mm, "end": v(-0.5, -2.34) * mm});
            skLineSegment(sketch, "E332", {"start": v(-0.5, -2.34) * mm, "end": v(-0.52, -2.28) * mm});
            skLineSegment(sketch, "E333", {"start": v(-0.52, -2.28) * mm, "end": v(-0.55, -2.22) * mm});
            skLineSegment(sketch, "E334", {"start": v(-0.55, -2.22) * mm, "end": v(-0.57, -2.17) * mm});
            skLineSegment(sketch, "E335", {"start": v(-0.57, -2.17) * mm, "end": v(-0.58, -2.1) * mm});
            skLineSegment(sketch, "E336", {"start": v(-0.58, -2.1) * mm, "end": v(-0.6, -2.05) * mm});
            skLineSegment(sketch, "E337", {"start": v(-0.6, -2.05) * mm, "end": v(-0.6, -1.99) * mm});
            skLineSegment(sketch, "E338", {"start": v(-0.6, -1.99) * mm, "end": v(-0.61, -1.92) * mm});
            skLineSegment(sketch, "E339", {"start": v(-0.61, -1.92) * mm, "end": v(-0.62, -1.86) * mm});
            skLineSegment(sketch, "E340", {"start": v(-0.62, -1.86) * mm, "end": v(-0.62, -1.8) * mm});
            skLineSegment(sketch, "E341", {"start": v(-0.62, -1.8) * mm, "end": v(-0.62, -1.74) * mm});
            skLineSegment(sketch, "E342", {"start": v(-0.62, -1.74) * mm, "end": v(-0.62, -1.68) * mm});
            skLineSegment(sketch, "E343", {"start": v(-0.62, -1.68) * mm, "end": v(-0.6, -1.62) * mm});
            skLineSegment(sketch, "E344", {"start": v(-0.6, -1.62) * mm, "end": v(-0.6, -1.56) * mm});
            skLineSegment(sketch, "E345", {"start": v(-0.6, -1.56) * mm, "end": v(-0.66, -1.56) * mm});
            skLineSegment(sketch, "E346", {"start": v(-0.66, -1.56) * mm, "end": v(-0.74, -1.57) * mm});
            skLineSegment(sketch, "E347", {"start": v(-0.74, -1.57) * mm, "end": v(-0.82, -1.58) * mm});
            skLineSegment(sketch, "E348", {"start": v(-0.82, -1.58) * mm, "end": v(-0.92, -1.6) * mm});
            skLineSegment(sketch, "E349", {"start": v(-0.92, -1.6) * mm, "end": v(-1.03, -1.63) * mm});
            skLineSegment(sketch, "E350", {"start": v(-1.03, -1.63) * mm, "end": v(-1.14, -1.67) * mm});
            skLineSegment(sketch, "E351", {"start": v(-1.14, -1.67) * mm, "end": v(-1.25, -1.71) * mm});
            skLineSegment(sketch, "E352", {"start": v(-1.25, -1.71) * mm, "end": v(-1.35, -1.77) * mm});
            skLineSegment(sketch, "E353", {"start": v(-1.35, -1.77) * mm, "end": v(-1.45, -1.82) * mm});
            skLineSegment(sketch, "E354", {"start": v(-1.45, -1.82) * mm, "end": v(-1.54, -1.89) * mm});
            skLineSegment(sketch, "E355", {"start": v(-1.54, -1.89) * mm, "end": v(-1.62, -1.95) * mm});
            skLineSegment(sketch, "E356", {"start": v(-1.62, -1.95) * mm, "end": v(-1.7, -2.03) * mm});
            skLineSegment(sketch, "E357", {"start": v(-1.7, -2.03) * mm, "end": v(-1.78, -2.1) * mm});
            skLineSegment(sketch, "E358", {"start": v(-1.78, -2.1) * mm, "end": v(-1.85, -2.2) * mm});
            skLineSegment(sketch, "E359", {"start": v(-1.85, -2.2) * mm, "end": v(-1.91, -2.28) * mm});
            skLineSegment(sketch, "E360", {"start": v(-1.91, -2.28) * mm, "end": v(-1.97, -2.37) * mm});
            skLineSegment(sketch, "E361", {"start": v(-1.97, -2.37) * mm, "end": v(-2.02, -2.46) * mm});
            skLineSegment(sketch, "E362", {"start": v(-2.02, -2.46) * mm, "end": v(-2.07, -2.56) * mm});
            skLineSegment(sketch, "E363", {"start": v(-2.07, -2.56) * mm, "end": v(-2.1, -2.66) * mm});
            skLineSegment(sketch, "E364", {"start": v(-2.1, -2.66) * mm, "end": v(-2.14, -2.76) * mm});
            skLineSegment(sketch, "E365", {"start": v(-2.14, -2.76) * mm, "end": v(-2.16, -2.87) * mm});
            skLineSegment(sketch, "E366", {"start": v(-2.16, -2.87) * mm, "end": v(-2.18, -2.97) * mm});
            skLineSegment(sketch, "E367", {"start": v(-2.18, -2.97) * mm, "end": v(-2.2, -3.08) * mm});
            skLineSegment(sketch, "E368", {"start": v(-2.2, -3.08) * mm, "end": v(-2.2, -3.2) * mm});
            skLineSegment(sketch, "E369", {"start": v(-2.2, -3.2) * mm, "end": v(-2.2, -3.3) * mm});
            skLineSegment(sketch, "E370", {"start": v(-2.2, -3.3) * mm, "end": v(-2.2, -3.4) * mm});
            skLineSegment(sketch, "E371", {"start": v(-2.2, -3.4) * mm, "end": v(-2.18, -3.52) * mm});
            skLineSegment(sketch, "E372", {"start": v(-2.18, -3.52) * mm, "end": v(-2.16, -3.62) * mm});
            skLineSegment(sketch, "E373", {"start": v(-2.16, -3.62) * mm, "end": v(-2.13, -3.73) * mm});
            skLineSegment(sketch, "E374", {"start": v(-2.13, -3.73) * mm, "end": v(-2.1, -3.84) * mm});
            skLineSegment(sketch, "E375", {"start": v(-2.1, -3.84) * mm, "end": v(-2.05, -3.94) * mm});
            skLineSegment(sketch, "E376", {"start": v(-2.05, -3.94) * mm, "end": v(-2, -4.04) * mm});
            skLineSegment(sketch, "E377", {"start": v(-2, -4.04) * mm, "end": v(-1.95, -4.14) * mm});
            skLineSegment(sketch, "E378", {"start": v(-1.95, -4.14) * mm, "end": v(-1.88, -4.24) * mm});
            skLineSegment(sketch, "E379", {"start": v(-1.88, -4.24) * mm, "end": v(-1.8, -4.33) * mm});
            skLineSegment(sketch, "E380", {"start": v(-1.8, -4.33) * mm, "end": v(-1.72, -4.42) * mm});
            skLineSegment(sketch, "E381", {"start": v(-1.72, -4.42) * mm, "end": v(-1.67, -4.48) * mm});
            skLineSegment(sketch, "E382", {"start": v(-1.67, -4.48) * mm, "end": v(-1.6, -4.53) * mm});
            skLineSegment(sketch, "E383", {"start": v(-1.6, -4.53) * mm, "end": v(-1.55, -4.58) * mm});
            skLineSegment(sketch, "E384", {"start": v(-1.55, -4.58) * mm, "end": v(-1.5, -4.63) * mm});
            skLineSegment(sketch, "E385", {"start": v(-1.5, -4.63) * mm, "end": v(-1.43, -4.67) * mm});
            skLineSegment(sketch, "E386", {"start": v(-1.43, -4.67) * mm, "end": v(-1.37, -4.71) * mm});
            skLineSegment(sketch, "E387", {"start": v(-1.37, -4.71) * mm, "end": v(-1.3, -4.75) * mm});
            skLineSegment(sketch, "E388", {"start": v(-1.3, -4.75) * mm, "end": v(-1.24, -4.78) * mm});
            skLineSegment(sketch, "E389", {"start": v(-1.24, -4.78) * mm, "end": v(-1.18, -4.81) * mm});
            skLineSegment(sketch, "E390", {"start": v(-1.18, -4.81) * mm, "end": v(-1.12, -4.84) * mm});
            skLineSegment(sketch, "E391", {"start": v(-1.12, -4.84) * mm, "end": v(-1.06, -4.86) * mm});
            skLineSegment(sketch, "E392", {"start": v(-1.06, -4.86) * mm, "end": v(-1, -4.88) * mm});
            skLineSegment(sketch, "E393", {"start": v(-1, -4.88) * mm, "end": v(-0.94, -4.9) * mm});
            skLineSegment(sketch, "E394", {"start": v(-0.94, -4.9) * mm, "end": v(-0.88, -4.91) * mm});
            skLineSegment(sketch, "E395", {"start": v(-0.88, -4.91) * mm, "end": v(-0.82, -4.92) * mm});
            skLineSegment(sketch, "E396", {"start": v(-0.82, -4.92) * mm, "end": v(-0.76, -4.93) * mm});
            skLineSegment(sketch, "E397", {"start": v(-0.76, -4.93) * mm, "end": v(-0.7, -4.94) * mm});
            skLineSegment(sketch, "E398", {"start": v(-0.7, -4.94) * mm, "end": v(-0.66, -4.94) * mm});
            skLineSegment(sketch, "E399", {"start": v(-0.66, -4.94) * mm, "end": v(-0.6, -4.93) * mm});
            skLineSegment(sketch, "E400", {"start": v(-0.6, -4.93) * mm, "end": v(-0.56, -4.93) * mm});
            skLineSegment(sketch, "E401", {"start": v(-0.56, -4.93) * mm, "end": v(-0.5, -4.92) * mm});
            skLineSegment(sketch, "E402", {"start": v(-0.5, -4.92) * mm, "end": v(-0.46, -4.9) * mm});
            skLineSegment(sketch, "E403", {"start": v(-0.46, -4.9) * mm, "end": v(-0.42, -4.89) * mm});
            skLineSegment(sketch, "E404", {"start": v(-0.42, -4.89) * mm, "end": v(-0.38, -4.87) * mm});
            skLineSegment(sketch, "E405", {"start": v(-0.38, -4.87) * mm, "end": v(-0.35, -4.84) * mm});
            skLineSegment(sketch, "E406", {"start": v(-0.35, -4.84) * mm, "end": v(-0.32, -4.82) * mm});
            skLineSegment(sketch, "E407", {"start": v(-0.32, -4.82) * mm, "end": v(-0.3, -4.79) * mm});
            skLineSegment(sketch, "E408", {"start": v(-0.3, -4.79) * mm, "end": v(-0.27, -4.75) * mm});
            skLineSegment(sketch, "E409", {"start": v(-0.27, -4.75) * mm, "end": v(-0.25, -4.72) * mm});
            skLineSegment(sketch, "E410", {"start": v(-0.25, -4.72) * mm, "end": v(-0.23, -4.67) * mm});
            skLineSegment(sketch, "E411", {"start": v(-0.23, -4.67) * mm, "end": v(-0.22, -4.63) * mm});
            skLineSegment(sketch, "E412", {"start": v(-0.22, -4.63) * mm, "end": v(-0.21, -4.58) * mm});
            skLineSegment(sketch, "E413", {"start": v(-0.21, -4.58) * mm, "end": v(-0.19, -4.5) * mm});
            skLineSegment(sketch, "E414", {"start": v(-0.19, -4.5) * mm, "end": v(-0.16, -4.4) * mm});
            skLineSegment(sketch, "E415", {"start": v(-0.16, -4.4) * mm, "end": v(-0.12, -4.33) * mm});
            skLineSegment(sketch, "E416", {"start": v(-0.12, -4.33) * mm, "end": v(-0.08, -4.25) * mm});
            skLineSegment(sketch, "E417", {"start": v(-0.08, -4.25) * mm, "end": v(-0.03, -4.18) * mm});
            skLineSegment(sketch, "E418", {"start": v(-0.03, -4.18) * mm, "end": v(0.03, -4.1) * mm});
            skLineSegment(sketch, "E419", {"start": v(0.03, -4.1) * mm, "end": v(0.1, -4.05) * mm});
            skLineSegment(sketch, "E420", {"start": v(0.1, -4.05) * mm, "end": v(0.16, -3.99) * mm});
            skLineSegment(sketch, "E421", {"start": v(0.16, -3.99) * mm, "end": v(0.23, -3.94) * mm});
            skLineSegment(sketch, "E422", {"start": v(0.23, -3.94) * mm, "end": v(0.3, -3.89) * mm});
            skLineSegment(sketch, "E423", {"start": v(0.3, -3.89) * mm, "end": v(0.38, -3.85) * mm});
            skLineSegment(sketch, "E424", {"start": v(0.38, -3.85) * mm, "end": v(0.47, -3.82) * mm});
            skLineSegment(sketch, "E425", {"start": v(0.47, -3.82) * mm, "end": v(0.55, -3.79) * mm});
            skLineSegment(sketch, "E426", {"start": v(0.55, -3.79) * mm, "end": v(0.64, -3.77) * mm});
            skLineSegment(sketch, "E427", {"start": v(0.64, -3.77) * mm, "end": v(0.73, -3.76) * mm});
            skLineSegment(sketch, "E428", {"start": v(0.73, -3.76) * mm, "end": v(0.82, -3.75) * mm});
            skLineSegment(sketch, "E429", {"start": v(0.82, -3.75) * mm, "end": v(0.88, -3.76) * mm});
            skLineSegment(sketch, "E430", {"start": v(0.88, -3.76) * mm, "end": v(0.93, -3.76) * mm});
            skLineSegment(sketch, "E431", {"start": v(0.93, -3.76) * mm, "end": v(0.98, -3.77) * mm});
            skLineSegment(sketch, "E432", {"start": v(0.98, -3.77) * mm, "end": v(1.04, -3.78) * mm});
            skLineSegment(sketch, "E433", {"start": v(1.04, -3.78) * mm, "end": v(1.09, -3.79) * mm});
            skLineSegment(sketch, "E434", {"start": v(1.09, -3.79) * mm, "end": v(1.14, -3.8) * mm});
            skLineSegment(sketch, "E435", {"start": v(1.14, -3.8) * mm, "end": v(1.19, -3.82) * mm});
            skLineSegment(sketch, "E436", {"start": v(1.19, -3.82) * mm, "end": v(1.24, -3.84) * mm});
            skLineSegment(sketch, "E437", {"start": v(1.24, -3.84) * mm, "end": v(1.33, -3.88) * mm});
            skLineSegment(sketch, "E438", {"start": v(1.33, -3.88) * mm, "end": v(1.42, -3.93) * mm});
            skLineSegment(sketch, "E439", {"start": v(1.42, -3.93) * mm, "end": v(1.5, -4) * mm});
            skLineSegment(sketch, "E440", {"start": v(1.5, -4) * mm, "end": v(1.57, -4.06) * mm});
            skLineSegment(sketch, "E441", {"start": v(1.57, -4.06) * mm, "end": v(1.64, -4.14) * mm});
            skLineSegment(sketch, "E442", {"start": v(1.64, -4.14) * mm, "end": v(1.7, -4.22) * mm});
            skLineSegment(sketch, "E443", {"start": v(1.7, -4.22) * mm, "end": v(1.75, -4.3) * mm});
            skLineSegment(sketch, "E444", {"start": v(1.75, -4.3) * mm, "end": v(1.8, -4.4) * mm});
            skLineSegment(sketch, "E445", {"start": v(1.8, -4.4) * mm, "end": v(1.82, -4.45) * mm});
            skLineSegment(sketch, "E446", {"start": v(1.82, -4.45) * mm, "end": v(1.83, -4.5) * mm});
            skLineSegment(sketch, "E447", {"start": v(1.83, -4.5) * mm, "end": v(1.85, -4.55) * mm});
            skLineSegment(sketch, "E448", {"start": v(1.85, -4.55) * mm, "end": v(1.86, -4.6) * mm});
            skLineSegment(sketch, "E449", {"start": v(1.86, -4.6) * mm, "end": v(1.87, -4.65) * mm});
            skLineSegment(sketch, "E450", {"start": v(1.87, -4.65) * mm, "end": v(1.88, -4.7) * mm});
            skLineSegment(sketch, "E451", {"start": v(1.88, -4.7) * mm, "end": v(1.88, -4.76) * mm});
            skLineSegment(sketch, "E452", {"start": v(1.88, -4.76) * mm, "end": v(1.88, -4.81) * mm});
            skLineSegment(sketch, "E453", {"start": v(1.88, -4.81) * mm, "end": v(1.88, -4.87) * mm});
            skLineSegment(sketch, "E454", {"start": v(1.88, -4.87) * mm, "end": v(1.88, -4.92) * mm});
            skLineSegment(sketch, "E455", {"start": v(1.88, -4.92) * mm, "end": v(1.87, -4.98) * mm});
            skLineSegment(sketch, "E456", {"start": v(1.87, -4.98) * mm, "end": v(1.86, -5.03) * mm});
            skLineSegment(sketch, "E457", {"start": v(1.86, -5.03) * mm, "end": v(1.85, -5.08) * mm});
            skLineSegment(sketch, "E458", {"start": v(1.85, -5.08) * mm, "end": v(1.83, -5.13) * mm});
            skLineSegment(sketch, "E459", {"start": v(1.83, -5.13) * mm, "end": v(1.82, -5.18) * mm});
            skLineSegment(sketch, "E460", {"start": v(1.82, -5.18) * mm, "end": v(1.8, -5.23) * mm});
            skLineSegment(sketch, "E461", {"start": v(1.8, -5.23) * mm, "end": v(1.78, -5.28) * mm});
            skLineSegment(sketch, "E462", {"start": v(1.78, -5.28) * mm, "end": v(1.75, -5.32) * mm});
            skLineSegment(sketch, "E463", {"start": v(1.75, -5.32) * mm, "end": v(1.7, -5.41) * mm});
            skLineSegment(sketch, "E464", {"start": v(1.7, -5.41) * mm, "end": v(1.63, -5.5) * mm});
            skLineSegment(sketch, "E465", {"start": v(1.63, -5.5) * mm, "end": v(1.56, -5.57) * mm});
            skLineSegment(sketch, "E466", {"start": v(1.56, -5.57) * mm, "end": v(1.56, -5.58) * mm});
            skLineSegment(sketch, "E467", {"start": v(1.56, -5.58) * mm, "end": v(1.46, -5.7) * mm});
            skLineSegment(sketch, "E468", {"start": v(1.46, -5.7) * mm, "end": v(1.4, -5.78) * mm});
            skLineSegment(sketch, "E469", {"start": v(1.4, -5.78) * mm, "end": v(1.35, -5.85) * mm});
            skLineSegment(sketch, "E470", {"start": v(1.35, -5.85) * mm, "end": v(1.22, -6.02) * mm});
            skLineSegment(sketch, "E471", {"start": v(1.22, -6.02) * mm, "end": v(1.17, -6.1) * mm});
            skLineSegment(sketch, "E472", {"start": v(1.17, -6.1) * mm, "end": v(1.12, -6.16) * mm});
            skLineSegment(sketch, "E473", {"start": v(1.12, -6.16) * mm, "end": v(1.09, -6.21) * mm});
            skLineSegment(sketch, "E474", {"start": v(1.09, -6.21) * mm, "end": v(1.06, -6.27) * mm});
            skLineSegment(sketch, "E475", {"start": v(1.06, -6.27) * mm, "end": v(1.04, -6.32) * mm});
            skLineSegment(sketch, "E476", {"start": v(1.04, -6.32) * mm, "end": v(1.03, -6.36) * mm});
            skLineSegment(sketch, "E477", {"start": v(1.03, -6.36) * mm, "end": v(1.03, -6.4) * mm});
            skLineSegment(sketch, "E478", {"start": v(1.03, -6.4) * mm, "end": v(1.04, -6.45) * mm});
            skLineSegment(sketch, "E479", {"start": v(1.04, -6.45) * mm, "end": v(1.06, -6.5) * mm});
            skLineSegment(sketch, "E480", {"start": v(1.06, -6.5) * mm, "end": v(1.08, -6.54) * mm});
            skLineSegment(sketch, "E481", {"start": v(1.08, -6.54) * mm, "end": v(1.11, -6.59) * mm});
            skLineSegment(sketch, "E482", {"start": v(1.11, -6.59) * mm, "end": v(1.15, -6.64) * mm});
            skLineSegment(sketch, "E483", {"start": v(1.15, -6.64) * mm, "end": v(1.26, -6.76) * mm});
            skLineSegment(sketch, "E484", {"start": v(1.26, -6.76) * mm, "end": v(1.3, -6.82) * mm});
            skLineSegment(sketch, "E485", {"start": v(1.3, -6.82) * mm, "end": v(1.35, -6.88) * mm});
            skLineSegment(sketch, "E486", {"start": v(1.35, -6.88) * mm, "end": v(1.39, -6.94) * mm});
            skLineSegment(sketch, "E487", {"start": v(1.39, -6.94) * mm, "end": v(1.42, -7) * mm});
            skLineSegment(sketch, "E488", {"start": v(1.42, -7) * mm, "end": v(1.46, -7.08) * mm});
            skLineSegment(sketch, "E489", {"start": v(1.46, -7.08) * mm, "end": v(1.5, -7.15) * mm});
            skLineSegment(sketch, "E490", {"start": v(1.5, -7.15) * mm, "end": v(1.52, -7.23) * mm});
            skLineSegment(sketch, "E491", {"start": v(1.52, -7.23) * mm, "end": v(1.55, -7.3) * mm});
            skLineSegment(sketch, "E492", {"start": v(1.55, -7.3) * mm, "end": v(1.58, -7.39) * mm});
            skLineSegment(sketch, "E493", {"start": v(1.58, -7.39) * mm, "end": v(1.6, -7.47) * mm});
            skLineSegment(sketch, "E494", {"start": v(1.6, -7.47) * mm, "end": v(1.62, -7.56) * mm});
            skLineSegment(sketch, "E495", {"start": v(1.62, -7.56) * mm, "end": v(1.64, -7.64) * mm});
            skLineSegment(sketch, "E496", {"start": v(1.64, -7.64) * mm, "end": v(1.66, -7.73) * mm});
            skLineSegment(sketch, "E497", {"start": v(1.66, -7.73) * mm, "end": v(1.67, -7.82) * mm});
            skLineSegment(sketch, "E498", {"start": v(1.67, -7.82) * mm, "end": v(1.68, -7.91) * mm});
            skLineSegment(sketch, "E499", {"start": v(1.68, -7.91) * mm, "end": v(1.69, -8) * mm});
            skLineSegment(sketch, "E500", {"start": v(1.69, -8) * mm, "end": v(1.7, -8.1) * mm});
            skLineSegment(sketch, "E501", {"start": v(1.7, -8.1) * mm, "end": v(1.7, -8.19) * mm});
            skLineSegment(sketch, "E502", {"start": v(1.7, -8.19) * mm, "end": v(1.7, -8.28) * mm});
            skLineSegment(sketch, "E503", {"start": v(1.7, -8.28) * mm, "end": v(1.7, -8.37) * mm});
            skLineSegment(sketch, "E504", {"start": v(1.7, -8.37) * mm, "end": v(1.69, -8.47) * mm});
            skLineSegment(sketch, "E505", {"start": v(1.69, -8.47) * mm, "end": v(1.68, -8.56) * mm});
            skLineSegment(sketch, "E506", {"start": v(1.68, -8.56) * mm, "end": v(1.67, -8.65) * mm});
            skLineSegment(sketch, "E507", {"start": v(1.67, -8.65) * mm, "end": v(1.66, -8.74) * mm});
            skLineSegment(sketch, "E508", {"start": v(1.66, -8.74) * mm, "end": v(1.64, -8.83) * mm});
            skLineSegment(sketch, "E509", {"start": v(1.64, -8.83) * mm, "end": v(1.62, -8.92) * mm});
            skLineSegment(sketch, "E510", {"start": v(1.62, -8.92) * mm, "end": v(1.6, -9) * mm});
            skLineSegment(sketch, "E511", {"start": v(1.6, -9) * mm, "end": v(1.57, -9.09) * mm});
            skLineSegment(sketch, "E512", {"start": v(1.57, -9.09) * mm, "end": v(1.55, -9.17) * mm});
            skLineSegment(sketch, "E513", {"start": v(1.55, -9.17) * mm, "end": v(1.52, -9.25) * mm});
            skLineSegment(sketch, "E514", {"start": v(1.52, -9.25) * mm, "end": v(1.48, -9.32) * mm});
            skLineSegment(sketch, "E515", {"start": v(1.48, -9.32) * mm, "end": v(1.45, -9.4) * mm});
            skLineSegment(sketch, "E516", {"start": v(1.45, -9.4) * mm, "end": v(1.36, -9.56) * mm});
            skLineSegment(sketch, "E517", {"start": v(1.36, -9.56) * mm, "end": v(1.3, -9.7) * mm});
            skLineSegment(sketch, "E518", {"start": v(1.3, -9.7) * mm, "end": v(1.28, -9.76) * mm});
            skLineSegment(sketch, "E519", {"start": v(1.28, -9.76) * mm, "end": v(1.26, -9.81) * mm});
            skLineSegment(sketch, "E520", {"start": v(1.26, -9.81) * mm, "end": v(1.24, -9.86) * mm});
            skLineSegment(sketch, "E521", {"start": v(1.24, -9.86) * mm, "end": v(1.24, -9.9) * mm});
            skLineSegment(sketch, "E522", {"start": v(1.24, -9.9) * mm, "end": v(1.2, -10.2) * mm});
            skLineSegment(sketch, "E523", {"start": v(1.2, -10.2) * mm, "end": v(1.15, -10.6) * mm});
            skLineSegment(sketch, "E524", {"start": v(1.15, -10.6) * mm, "end": v(1.1, -11.1) * mm});
            skLineSegment(sketch, "E525", {"start": v(1.1, -11.1) * mm, "end": v(1.06, -11.65) * mm});
            skLineSegment(sketch, "E526", {"start": v(1.06, -11.65) * mm, "end": v(0.95, -12.88) * mm});
            skLineSegment(sketch, "E527", {"start": v(0.95, -12.88) * mm, "end": v(0.85, -14.2) * mm});
            skLineSegment(sketch, "E528", {"start": v(0.85, -14.2) * mm, "end": v(0.85, -14.33) * mm});
            skLineSegment(sketch, "E529", {"start": v(0.85, -14.33) * mm, "end": v(0.98, -14.38) * mm});
            skLineSegment(sketch, "E530", {"start": v(0.98, -14.38) * mm, "end": v(1.1, -14.43) * mm});
            skLineSegment(sketch, "E531", {"start": v(1.1, -14.43) * mm, "end": v(1.23, -14.5) * mm});
            skLineSegment(sketch, "E532", {"start": v(1.23, -14.5) * mm, "end": v(1.34, -14.57) * mm});
            skLineSegment(sketch, "E533", {"start": v(1.34, -14.57) * mm, "end": v(1.46, -14.65) * mm});
            skLineSegment(sketch, "E534", {"start": v(1.46, -14.65) * mm, "end": v(1.57, -14.74) * mm});
            skLineSegment(sketch, "E535", {"start": v(1.57, -14.74) * mm, "end": v(1.67, -14.83) * mm});
            skLineSegment(sketch, "E536", {"start": v(1.67, -14.83) * mm, "end": v(1.77, -14.93) * mm});
            skLineSegment(sketch, "E537", {"start": v(1.77, -14.93) * mm, "end": v(1.86, -15.04) * mm});
            skLineSegment(sketch, "E538", {"start": v(1.86, -15.04) * mm, "end": v(1.94, -15.15) * mm});
            skLineSegment(sketch, "E539", {"start": v(1.94, -15.15) * mm, "end": v(2.02, -15.26) * mm});
            skLineSegment(sketch, "E540", {"start": v(2.02, -15.26) * mm, "end": v(2.08, -15.38) * mm});
            skLineSegment(sketch, "E541", {"start": v(2.08, -15.38) * mm, "end": v(2.15, -15.5) * mm});
            skLineSegment(sketch, "E542", {"start": v(2.15, -15.5) * mm, "end": v(2.2, -15.64) * mm});
            skLineSegment(sketch, "E543", {"start": v(2.2, -15.64) * mm, "end": v(2.24, -15.77) * mm});
            skLineSegment(sketch, "E544", {"start": v(2.24, -15.77) * mm, "end": v(2.28, -15.9) * mm});
            skLineSegment(sketch, "E545", {"start": v(2.28, -15.9) * mm, "end": v(2.3, -16.04) * mm});
            skLineSegment(sketch, "E546", {"start": v(2.3, -16.04) * mm, "end": v(2.33, -16.18) * mm});
            skLineSegment(sketch, "E547", {"start": v(2.33, -16.18) * mm, "end": v(2.34, -16.31) * mm});
            skLineSegment(sketch, "E548", {"start": v(2.34, -16.31) * mm, "end": v(2.34, -16.45) * mm});
            skLineSegment(sketch, "E549", {"start": v(2.34, -16.45) * mm, "end": v(2.34, -16.6) * mm});
            skLineSegment(sketch, "E550", {"start": v(2.34, -16.6) * mm, "end": v(2.32, -16.73) * mm});
            skLineSegment(sketch, "E551", {"start": v(2.32, -16.73) * mm, "end": v(2.3, -16.87) * mm});
            skLineSegment(sketch, "E552", {"start": v(2.3, -16.87) * mm, "end": v(2.26, -17) * mm});
            skLineSegment(sketch, "E553", {"start": v(2.26, -17) * mm, "end": v(2.22, -17.13) * mm});
            skLineSegment(sketch, "E554", {"start": v(2.22, -17.13) * mm, "end": v(2.17, -17.26) * mm});
            skLineSegment(sketch, "E555", {"start": v(2.17, -17.26) * mm, "end": v(2.12, -17.4) * mm});
            skLineSegment(sketch, "E556", {"start": v(2.12, -17.4) * mm, "end": v(2.05, -17.51) * mm});
            skLineSegment(sketch, "E557", {"start": v(2.05, -17.51) * mm, "end": v(1.98, -17.63) * mm});
            skLineSegment(sketch, "E558", {"start": v(1.98, -17.63) * mm, "end": v(1.9, -17.75) * mm});
            skLineSegment(sketch, "E559", {"start": v(1.9, -17.75) * mm, "end": v(1.81, -17.85) * mm});
            skLineSegment(sketch, "E560", {"start": v(1.81, -17.85) * mm, "end": v(1.72, -17.96) * mm});
            skLineSegment(sketch, "E561", {"start": v(1.72, -17.96) * mm, "end": v(1.62, -18.05) * mm});
            skLineSegment(sketch, "E562", {"start": v(1.62, -18.05) * mm, "end": v(1.51, -18.14) * mm});
            skLineSegment(sketch, "E563", {"start": v(1.51, -18.14) * mm, "end": v(1.4, -18.23) * mm});
            skLineSegment(sketch, "E564", {"start": v(1.4, -18.23) * mm, "end": v(1.29, -18.3) * mm});
            skLineSegment(sketch, "E565", {"start": v(1.29, -18.3) * mm, "end": v(1.17, -18.37) * mm});
            skLineSegment(sketch, "E566", {"start": v(1.17, -18.37) * mm, "end": v(1.04, -18.43) * mm});
            skLineSegment(sketch, "E567", {"start": v(1.04, -18.43) * mm, "end": v(0.91, -18.49) * mm});
            skLineSegment(sketch, "E568", {"start": v(0.91, -18.49) * mm, "end": v(0.85, -18.51) * mm});
            skLineSegment(sketch, "E569", {"start": v(0.85, -18.51) * mm, "end": v(0.75, -19.9) * mm});
            skLineSegment(sketch, "E570", {"start": v(0.75, -19.9) * mm, "end": v(0.59, -29.47) * mm});
            skLineSegment(sketch, "E571", {"start": v(0.59, -29.47) * mm, "end": v(0.59, -29.49) * mm});
            skLineSegment(sketch, "E572", {"start": v(0.59, -29.49) * mm, "end": v(0.59, -29.5) * mm});
            skLineSegment(sketch, "E573", {"start": v(0.59, -29.5) * mm, "end": v(0.59, -29.52) * mm});
            skLineSegment(sketch, "E574", {"start": v(0.59, -29.52) * mm, "end": v(0.58, -29.54) * mm});
            skLineSegment(sketch, "E575", {"start": v(0.58, -29.54) * mm, "end": v(0.58, -29.55) * mm});
            skLineSegment(sketch, "E576", {"start": v(0.58, -29.55) * mm, "end": v(0.58, -29.57) * mm});
            skLineSegment(sketch, "E577", {"start": v(0.58, -29.57) * mm, "end": v(0.58, -29.59) * mm});
            skLineSegment(sketch, "E578", {"start": v(0.58, -29.59) * mm, "end": v(0.57, -29.6) * mm});
            skLineSegment(sketch, "E579", {"start": v(0.57, -29.6) * mm, "end": v(0.57, -29.62) * mm});
            skLineSegment(sketch, "E580", {"start": v(0.57, -29.62) * mm, "end": v(0.56, -29.64) * mm});
            skLineSegment(sketch, "E581", {"start": v(0.56, -29.64) * mm, "end": v(0.56, -29.66) * mm});
            skLineSegment(sketch, "E582", {"start": v(0.56, -29.66) * mm, "end": v(0.55, -29.67) * mm});
            skLineSegment(sketch, "E583", {"start": v(0.55, -29.67) * mm, "end": v(0.54, -29.69) * mm});
            skLineSegment(sketch, "E584", {"start": v(0.54, -29.69) * mm, "end": v(0.54, -29.7) * mm});
            skLineSegment(sketch, "E585", {"start": v(0.54, -29.7) * mm, "end": v(0.53, -29.72) * mm});
            skLineSegment(sketch, "E586", {"start": v(0.53, -29.72) * mm, "end": v(0.52, -29.74) * mm});
            skLineSegment(sketch, "E587", {"start": v(0.52, -29.74) * mm, "end": v(0.51, -29.75) * mm});
            skLineSegment(sketch, "E588", {"start": v(0.51, -29.75) * mm, "end": v(0.5, -29.77) * mm});
            skLineSegment(sketch, "E589", {"start": v(0.5, -29.77) * mm, "end": v(0.5, -29.78) * mm});
            skLineSegment(sketch, "E590", {"start": v(0.5, -29.78) * mm, "end": v(0.48, -29.8) * mm});
            skLineSegment(sketch, "E591", {"start": v(0.48, -29.8) * mm, "end": v(0.47, -29.8) * mm});
            skLineSegment(sketch, "E592", {"start": v(0.47, -29.8) * mm, "end": v(0.46, -29.82) * mm});
            skLineSegment(sketch, "E593", {"start": v(0.46, -29.82) * mm, "end": v(0.45, -29.84) * mm});
            skLineSegment(sketch, "E594", {"start": v(0.45, -29.84) * mm, "end": v(0.44, -29.85) * mm});
            skLineSegment(sketch, "E595", {"start": v(0.44, -29.85) * mm, "end": v(0.43, -29.86) * mm});
            skLineSegment(sketch, "E596", {"start": v(0.43, -29.86) * mm, "end": v(0.42, -29.87) * mm});
            skLineSegment(sketch, "E597", {"start": v(0.42, -29.87) * mm, "end": v(0.4, -29.88) * mm});
            skLineSegment(sketch, "E598", {"start": v(0.4, -29.88) * mm, "end": v(0.4, -29.9) * mm});
            skLineSegment(sketch, "E599", {"start": v(0.4, -29.9) * mm, "end": v(0.38, -29.9) * mm});
            skLineSegment(sketch, "E600", {"start": v(0.38, -29.9) * mm, "end": v(0.36, -29.92) * mm});
            skLineSegment(sketch, "E601", {"start": v(0.36, -29.92) * mm, "end": v(0.35, -29.93) * mm});
            skLineSegment(sketch, "E602", {"start": v(0.35, -29.93) * mm, "end": v(0.33, -29.94) * mm});
            skLineSegment(sketch, "E603", {"start": v(0.33, -29.94) * mm, "end": v(0.32, -29.95) * mm});
            skLineSegment(sketch, "E604", {"start": v(0.32, -29.95) * mm, "end": v(0.3, -29.96) * mm});
            skLineSegment(sketch, "E605", {"start": v(0.3, -29.96) * mm, "end": v(0.29, -29.96) * mm});
            skLineSegment(sketch, "E606", {"start": v(0.29, -29.96) * mm, "end": v(0.27, -29.97) * mm});
            skLineSegment(sketch, "E607", {"start": v(0.27, -29.97) * mm, "end": v(0.26, -29.98) * mm});
            skLineSegment(sketch, "E608", {"start": v(0.26, -29.98) * mm, "end": v(0.24, -29.99) * mm});
            skLineSegment(sketch, "E609", {"start": v(0.24, -29.99) * mm, "end": v(0.23, -30) * mm});
            skLineSegment(sketch, "E610", {"start": v(0.23, -30) * mm, "end": v(0.2, -30) * mm});
            skLineSegment(sketch, "E611", {"start": v(0.2, -30) * mm, "end": v(0.2, -30) * mm});
            skLineSegment(sketch, "E612", {"start": v(0.2, -30) * mm, "end": v(0.18, -30) * mm});
            skLineSegment(sketch, "E613", {"start": v(0.18, -30) * mm, "end": v(0.16, -30.01) * mm});
            skLineSegment(sketch, "E614", {"start": v(0.16, -30.01) * mm, "end": v(0.14, -30.02) * mm});
            skLineSegment(sketch, "E615", {"start": v(0.14, -30.02) * mm, "end": v(0.12, -30.02) * mm});
            skLineSegment(sketch, "E616", {"start": v(0.12, -30.02) * mm, "end": v(0.1, -30.02) * mm});
            skLineSegment(sketch, "E617", {"start": v(0.1, -30.02) * mm, "end": v(0.09, -30.02) * mm});
            skLineSegment(sketch, "E618", {"start": v(0.09, -30.02) * mm, "end": v(0.07, -30.02) * mm});
            skLineSegment(sketch, "E619", {"start": v(0.07, -30.02) * mm, "end": v(0.05, -30.03) * mm});
            skLineSegment(sketch, "E620", {"start": v(0.05, -30.03) * mm, "end": v(0.04, -30.03) * mm});
            skLineSegment(sketch, "E621", {"start": v(0.04, -30.03) * mm, "end": v(0.02, -30.03) * mm});
            skLineSegment(sketch, "E622", {"start": v(0.02, -30.03) * mm, "end": v(0, -30.02) * mm});
            skLineSegment(sketch, "E623", {"start": v(0, -30.02) * mm, "end": v(-0.01, -30.02) * mm});
            skLineSegment(sketch, "E624", {"start": v(-0.01, -30.02) * mm, "end": v(-0.03, -30.02) * mm});
            skLineSegment(sketch, "E625", {"start": v(-0.03, -30.02) * mm, "end": v(-0.05, -30.02) * mm});
            skLineSegment(sketch, "E626", {"start": v(-0.05, -30.02) * mm, "end": v(-0.07, -30.02) * mm});
            skLineSegment(sketch, "E627", {"start": v(-0.07, -30.02) * mm, "end": v(-0.08, -30.01) * mm});
            skLineSegment(sketch, "E628", {"start": v(-0.08, -30.01) * mm, "end": v(-0.1, -30) * mm});
            skLineSegment(sketch, "E629", {"start": v(-0.1, -30) * mm, "end": v(-0.12, -30) * mm});
            skLineSegment(sketch, "E630", {"start": v(-0.12, -30) * mm, "end": v(-0.13, -30) * mm});
            skLineSegment(sketch, "E631", {"start": v(-0.13, -30) * mm, "end": v(-0.15, -30) * mm});
            skLineSegment(sketch, "E632", {"start": v(-0.15, -30) * mm, "end": v(-0.17, -29.99) * mm});
            skLineSegment(sketch, "E633", {"start": v(-0.17, -29.99) * mm, "end": v(-0.18, -29.98) * mm});
            skLineSegment(sketch, "E634", {"start": v(-0.18, -29.98) * mm, "end": v(-0.2, -29.97) * mm});
            skLineSegment(sketch, "E635", {"start": v(-0.2, -29.97) * mm, "end": v(-0.21, -29.97) * mm});
            skLineSegment(sketch, "E636", {"start": v(-0.21, -29.97) * mm, "end": v(-0.23, -29.96) * mm});
            skLineSegment(sketch, "E637", {"start": v(-0.23, -29.96) * mm, "end": v(-0.25, -29.95) * mm});
            skLineSegment(sketch, "E638", {"start": v(-0.25, -29.95) * mm, "end": v(-0.26, -29.94) * mm});
            skLineSegment(sketch, "E639", {"start": v(-0.26, -29.94) * mm, "end": v(-0.27, -29.93) * mm});
            skLineSegment(sketch, "E640", {"start": v(-0.27, -29.93) * mm, "end": v(-0.29, -29.92) * mm});
            skLineSegment(sketch, "E641", {"start": v(-0.29, -29.92) * mm, "end": v(-0.3, -29.91) * mm});
            skLineSegment(sketch, "E642", {"start": v(-0.3, -29.91) * mm, "end": v(-0.32, -29.9) * mm});
            skLineSegment(sketch, "E643", {"start": v(-0.32, -29.9) * mm, "end": v(-0.33, -29.89) * mm});
            skLineSegment(sketch, "E644", {"start": v(-0.33, -29.89) * mm, "end": v(-0.34, -29.88) * mm});
            skLineSegment(sketch, "E645", {"start": v(-0.34, -29.88) * mm, "end": v(-0.36, -29.87) * mm});
            skLineSegment(sketch, "E646", {"start": v(-0.36, -29.87) * mm, "end": v(-0.37, -29.85) * mm});
            skLineSegment(sketch, "E647", {"start": v(-0.37, -29.85) * mm, "end": v(-0.38, -29.84) * mm});
            skLineSegment(sketch, "E648", {"start": v(-0.38, -29.84) * mm, "end": v(-0.4, -29.83) * mm});
            skLineSegment(sketch, "E649", {"start": v(-0.4, -29.83) * mm, "end": v(-0.4, -29.81) * mm});
            skLineSegment(sketch, "E650", {"start": v(-0.4, -29.81) * mm, "end": v(-0.41, -29.8) * mm});
            skLineSegment(sketch, "E651", {"start": v(-0.41, -29.8) * mm, "end": v(-0.42, -29.79) * mm});
            skLineSegment(sketch, "E652", {"start": v(-0.42, -29.79) * mm, "end": v(-0.43, -29.77) * mm});
            skLineSegment(sketch, "E653", {"start": v(-0.43, -29.77) * mm, "end": v(-0.44, -29.76) * mm});
            skLineSegment(sketch, "E654", {"start": v(-0.44, -29.76) * mm, "end": v(-0.45, -29.74) * mm});
            skLineSegment(sketch, "E655", {"start": v(-0.45, -29.74) * mm, "end": v(-0.46, -29.73) * mm});
            skLineSegment(sketch, "E656", {"start": v(-0.46, -29.73) * mm, "end": v(-0.47, -29.71) * mm});
            skLineSegment(sketch, "E657", {"start": v(-0.47, -29.71) * mm, "end": v(-0.47, -29.7) * mm});
            skLineSegment(sketch, "E658", {"start": v(-0.47, -29.7) * mm, "end": v(-0.48, -29.68) * mm});
            skLineSegment(sketch, "E659", {"start": v(-0.48, -29.68) * mm, "end": v(-0.49, -29.66) * mm});
            skLineSegment(sketch, "E660", {"start": v(-0.49, -29.66) * mm, "end": v(-0.5, -29.65) * mm});
            skLineSegment(sketch, "E661", {"start": v(-0.5, -29.65) * mm, "end": v(-0.5, -29.63) * mm});
            skLineSegment(sketch, "E662", {"start": v(-0.5, -29.63) * mm, "end": v(-0.5, -29.61) * mm});
            skLineSegment(sketch, "E663", {"start": v(-0.5, -29.61) * mm, "end": v(-0.5, -29.6) * mm});
            skLineSegment(sketch, "E664", {"start": v(-0.5, -29.6) * mm, "end": v(-0.51, -29.58) * mm});
            skLineSegment(sketch, "E665", {"start": v(-0.51, -29.58) * mm, "end": v(-0.51, -29.56) * mm});
            skLineSegment(sketch, "E666", {"start": v(-0.51, -29.56) * mm, "end": v(-0.52, -29.54) * mm});
            skLineSegment(sketch, "E667", {"start": v(-0.52, -29.54) * mm, "end": v(-0.52, -29.53) * mm});
            skLineSegment(sketch, "E668", {"start": v(-0.52, -29.53) * mm, "end": v(-0.52, -29.5) * mm});
            skLineSegment(sketch, "E669", {"start": v(-0.52, -29.5) * mm, "end": v(-0.52, -29.5) * mm});
            skLineSegment(sketch, "E670", {"start": v(-0.52, -29.5) * mm, "end": v(-0.8, -20) * mm});
            skLineSegment(sketch, "E671", {"start": v(-0.8, -20) * mm, "end": v(-0.81, -18.79) * mm});
            skLineSegment(sketch, "E672", {"start": v(-0.81, -18.79) * mm, "end": v(-0.81, -18.42) * mm});
            skLineSegment(sketch, "E673", {"start": v(-0.81, -18.42) * mm, "end": v(-0.94, -18.36) * mm});
            skLineSegment(sketch, "E674", {"start": v(-0.94, -18.36) * mm, "end": v(-1.06, -18.28) * mm});
            skLineSegment(sketch, "E675", {"start": v(-1.06, -18.28) * mm, "end": v(-1.17, -18.2) * mm});
            skLineSegment(sketch, "E676", {"start": v(-1.17, -18.2) * mm, "end": v(-1.28, -18.12) * mm});
            skLineSegment(sketch, "E677", {"start": v(-1.28, -18.12) * mm, "end": v(-1.39, -18.03) * mm});
            skLineSegment(sketch, "E678", {"start": v(-1.39, -18.03) * mm, "end": v(-1.48, -17.93) * mm});
            skLineSegment(sketch, "E679", {"start": v(-1.48, -17.93) * mm, "end": v(-1.58, -17.83) * mm});
            skLineSegment(sketch, "E680", {"start": v(-1.58, -17.83) * mm, "end": v(-1.66, -17.72) * mm});
            skLineSegment(sketch, "E681", {"start": v(-1.66, -17.72) * mm, "end": v(-1.74, -17.6) * mm});
            skLineSegment(sketch, "E682", {"start": v(-1.74, -17.6) * mm, "end": v(-1.8, -17.48) * mm});
            skLineSegment(sketch, "E683", {"start": v(-1.8, -17.48) * mm, "end": v(-1.87, -17.36) * mm});
            skLineSegment(sketch, "E684", {"start": v(-1.87, -17.36) * mm, "end": v(-1.93, -17.23) * mm});
            skLineSegment(sketch, "E685", {"start": v(-1.93, -17.23) * mm, "end": v(-1.97, -17.1) * mm});
            skLineSegment(sketch, "E686", {"start": v(-1.97, -17.1) * mm, "end": v(-2.01, -16.97) * mm});
            skLineSegment(sketch, "E687", {"start": v(-2.01, -16.97) * mm, "end": v(-2.04, -16.83) * mm});
            skLineSegment(sketch, "E688", {"start": v(-2.04, -16.83) * mm, "end": v(-2.06, -16.7) * mm});
            skLineSegment(sketch, "E689", {"start": v(-2.06, -16.7) * mm, "end": v(-2.08, -16.55) * mm});
            skLineSegment(sketch, "E690", {"start": v(-2.08, -16.55) * mm, "end": v(-2.08, -16.42) * mm});
            skLineSegment(sketch, "E691", {"start": v(-2.08, -16.42) * mm, "end": v(-2.08, -16.28) * mm});
            skLineSegment(sketch, "E692", {"start": v(-2.08, -16.28) * mm, "end": v(-2.06, -16.14) * mm});
            skLineSegment(sketch, "E693", {"start": v(-2.06, -16.14) * mm, "end": v(-2.04, -16) * mm});
            skLineSegment(sketch, "E694", {"start": v(-2.04, -16) * mm, "end": v(-2, -15.87) * mm});
            skLineSegment(sketch, "E695", {"start": v(-2, -15.87) * mm, "end": v(-1.97, -15.73) * mm});
            skLineSegment(sketch, "E696", {"start": v(-1.97, -15.73) * mm, "end": v(-1.92, -15.6) * mm});
            skLineSegment(sketch, "E697", {"start": v(-1.92, -15.6) * mm, "end": v(-1.87, -15.47) * mm});
            skLineSegment(sketch, "E698", {"start": v(-1.87, -15.47) * mm, "end": v(-1.8, -15.35) * mm});
            skLineSegment(sketch, "E699", {"start": v(-1.8, -15.35) * mm, "end": v(-1.73, -15.23) * mm});
            skLineSegment(sketch, "E700", {"start": v(-1.73, -15.23) * mm, "end": v(-1.65, -15.12) * mm});
            skLineSegment(sketch, "E701", {"start": v(-1.65, -15.12) * mm, "end": v(-1.57, -15) * mm});
            skLineSegment(sketch, "E702", {"start": v(-1.57, -15) * mm, "end": v(-1.48, -14.9) * mm});
            skLineSegment(sketch, "E703", {"start": v(-1.48, -14.9) * mm, "end": v(-1.38, -14.8) * mm});
            skLineSegment(sketch, "E704", {"start": v(-1.38, -14.8) * mm, "end": v(-1.27, -14.71) * mm});
            skLineSegment(sketch, "E705", {"start": v(-1.27, -14.71) * mm, "end": v(-1.16, -14.63) * mm});
            skLineSegment(sketch, "E706", {"start": v(-1.16, -14.63) * mm, "end": v(-1.05, -14.55) * mm});
            skLineSegment(sketch, "E707", {"start": v(-1.05, -14.55) * mm, "end": v(-0.93, -14.48) * mm});
            skLineSegment(sketch, "E708", {"start": v(-0.93, -14.48) * mm, "end": v(-0.81, -14.42) * mm});
            skLineSegment(sketch, "E709", {"start": v(-0.81, -14.42) * mm, "end": v(-0.82, -13.12) * mm});
            skLineSegment(sketch, "E710", {"start": v(-0.82, -13.12) * mm, "end": v(-0.83, -12.53) * mm});
            skLineSegment(sketch, "E711", {"start": v(-0.83, -12.53) * mm, "end": v(-0.84, -11.97) * mm});
            skLineSegment(sketch, "E712", {"start": v(-0.84, -11.97) * mm, "end": v(-0.85, -11.45) * mm});
            skLineSegment(sketch, "E713", {"start": v(-0.85, -11.45) * mm, "end": v(-0.87, -11) * mm});
            skLineSegment(sketch, "E714", {"start": v(-0.87, -11) * mm, "end": v(-0.88, -10.63) * mm});
            skLineSegment(sketch, "E715", {"start": v(-0.88, -10.63) * mm, "end": v(-0.9, -10.34) * mm});
            skLineSegment(sketch, "E716", {"start": v(-0.9, -10.34) * mm, "end": v(-0.92, -10.26) * mm});
            skLineSegment(sketch, "E717", {"start": v(-0.92, -10.26) * mm, "end": v(-0.93, -10.2) * mm});
            skLineSegment(sketch, "E718", {"start": v(-0.93, -10.2) * mm, "end": v(-0.96, -10.13) * mm});
            skLineSegment(sketch, "E719", {"start": v(-0.96, -10.13) * mm, "end": v(-0.98, -10.07) * mm});
            skLineSegment(sketch, "E720", {"start": v(-0.98, -10.07) * mm, "end": v(-1.02, -10.02) * mm});
            skLineSegment(sketch, "E721", {"start": v(-1.02, -10.02) * mm, "end": v(-1.05, -9.97) * mm});
            skLineSegment(sketch, "E722", {"start": v(-1.05, -9.97) * mm, "end": v(-1.1, -9.92) * mm});
            skLineSegment(sketch, "E723", {"start": v(-1.1, -9.92) * mm, "end": v(-1.14, -9.88) * mm});
            skLineSegment(sketch, "E724", {"start": v(-1.14, -9.88) * mm, "end": v(-1.22, -9.8) * mm});
            skLineSegment(sketch, "E725", {"start": v(-1.22, -9.8) * mm, "end": v(-1.31, -9.72) * mm});
            skLineSegment(sketch, "E726", {"start": v(-1.31, -9.72) * mm, "end": v(-1.4, -9.65) * mm});
            skLineSegment(sketch, "E727", {"start": v(-1.4, -9.65) * mm, "end": v(-1.44, -9.61) * mm});
            skLineSegment(sketch, "E728", {"start": v(-1.44, -9.61) * mm, "end": v(-1.48, -9.57) * mm});
            skLineSegment(sketch, "E729", {"start": v(-1.48, -9.57) * mm, "end": v(-1.48, -9.57) * mm});
            skLineSegment(sketch, "E730", {"start": v(-1.48, -9.57) * mm, "end": v(-1.61, -9.46) * mm});
            skLineSegment(sketch, "E731", {"start": v(-1.61, -9.46) * mm, "end": v(-1.68, -9.41) * mm});
            skLineSegment(sketch, "E732", {"start": v(-1.68, -9.41) * mm, "end": v(-1.74, -9.36) * mm});
            skLineSegment(sketch, "E733", {"start": v(-1.74, -9.36) * mm, "end": v(-1.8, -9.3) * mm});
            skLineSegment(sketch, "E734", {"start": v(-1.8, -9.3) * mm, "end": v(-1.84, -9.25) * mm});
            skLineSegment(sketch, "E735", {"start": v(-1.84, -9.25) * mm, "end": v(-1.89, -9.2) * mm});
            skLineSegment(sketch, "E736", {"start": v(-1.89, -9.2) * mm, "end": v(-1.93, -9.14) * mm});
            skLineSegment(sketch, "E737", {"start": v(-1.93, -9.14) * mm, "end": v(-1.97, -9.08) * mm});
            skLineSegment(sketch, "E738", {"start": v(-1.97, -9.08) * mm, "end": v(-2, -9.02) * mm});
            skLineSegment(sketch, "E739", {"start": v(-2, -9.02) * mm, "end": v(-2.03, -8.95) * mm});
            skLineSegment(sketch, "E740", {"start": v(-2.03, -8.95) * mm, "end": v(-2.06, -8.89) * mm});
            skLineSegment(sketch, "E741", {"start": v(-2.06, -8.89) * mm, "end": v(-2.07, -8.82) * mm});
            skLineSegment(sketch, "E742", {"start": v(-2.07, -8.82) * mm, "end": v(-2.09, -8.75) * mm});
            skLineSegment(sketch, "E743", {"start": v(-2.09, -8.75) * mm, "end": v(-2.1, -8.67) * mm});
            skLineSegment(sketch, "E744", {"start": v(-2.1, -8.67) * mm, "end": v(-2.1, -8.6) * mm});
            skLineSegment(sketch, "E745", {"start": v(-2.1, -8.6) * mm, "end": v(-2.1, -8.54) * mm});
            skLineSegment(sketch, "E746", {"start": v(-2.1, -8.54) * mm, "end": v(-2.1, -8.48) * mm});
            skLineSegment(sketch, "E747", {"start": v(-2.1, -8.48) * mm, "end": v(-2.09, -8.43) * mm});
            skLineSegment(sketch, "E748", {"start": v(-2.09, -8.43) * mm, "end": v(-2.08, -8.37) * mm});
            skLineSegment(sketch, "E749", {"start": v(-2.08, -8.37) * mm, "end": v(-2.06, -8.32) * mm});
            skLineSegment(sketch, "E750", {"start": v(-2.06, -8.32) * mm, "end": v(-2.05, -8.27) * mm});
            skLineSegment(sketch, "E751", {"start": v(-2.05, -8.27) * mm, "end": v(-2.03, -8.22) * mm});
            skLineSegment(sketch, "E752", {"start": v(-2.03, -8.22) * mm, "end": v(-2.01, -8.17) * mm});
            skLineSegment(sketch, "E753", {"start": v(-2.01, -8.17) * mm, "end": v(-2, -8.12) * mm});
            skLineSegment(sketch, "E754", {"start": v(-2, -8.12) * mm, "end": v(-1.97, -8.08) * mm});
            skLineSegment(sketch, "E755", {"start": v(-1.97, -8.08) * mm, "end": v(-1.91, -7.99) * mm});
            skLineSegment(sketch, "E756", {"start": v(-1.91, -7.99) * mm, "end": v(-1.85, -7.9) * mm});
            skLineSegment(sketch, "E757", {"start": v(-1.85, -7.9) * mm, "end": v(-1.78, -7.83) * mm});
            skLineSegment(sketch, "E758", {"start": v(-1.78, -7.83) * mm, "end": v(-1.7, -7.76) * mm});
            skLineSegment(sketch, "E759", {"start": v(-1.7, -7.76) * mm, "end": v(-1.62, -7.7) * mm});
            skLineSegment(sketch, "E760", {"start": v(-1.62, -7.7) * mm, "end": v(-1.53, -7.64) * mm});
            skLineSegment(sketch, "E761", {"start": v(-1.53, -7.64) * mm, "end": v(-1.49, -7.62) * mm});
            skLineSegment(sketch, "E762", {"start": v(-1.49, -7.62) * mm, "end": v(-1.44, -7.6) * mm});
            skLineSegment(sketch, "E763", {"start": v(-1.44, -7.6) * mm, "end": v(-1.39, -7.58) * mm});
            skLineSegment(sketch, "E764", {"start": v(-1.39, -7.58) * mm, "end": v(-1.34, -7.56) * mm});
            skLineSegment(sketch, "E765", {"start": v(-1.34, -7.56) * mm, "end": v(-1.29, -7.54) * mm});
            skLineSegment(sketch, "E766", {"start": v(-1.29, -7.54) * mm, "end": v(-1.23, -7.53) * mm});
            skLineSegment(sketch, "E767", {"start": v(-1.23, -7.53) * mm, "end": v(-1.18, -7.52) * mm});
            skLineSegment(sketch, "E768", {"start": v(-1.18, -7.52) * mm, "end": v(-1.13, -7.51) * mm});
            skLineSegment(sketch, "E769", {"start": v(-1.13, -7.51) * mm, "end": v(-1.07, -7.51) * mm});
            skLineSegment(sketch, "E770", {"start": v(-1.07, -7.51) * mm, "end": v(-1.02, -7.5) * mm});
            skLineSegment(sketch, "E771", {"start": v(-1.02, -7.5) * mm, "end": v(-0.96, -7.51) * mm});
            skLineSegment(sketch, "E772", {"start": v(-0.96, -7.51) * mm, "end": v(-0.9, -7.51) * mm});
            skLineSegment(sketch, "E773", {"start": v(-0.9, -7.51) * mm, "end": v(-0.85, -7.52) * mm});
            skLineSegment(sketch, "E774", {"start": v(-0.85, -7.52) * mm, "end": v(-0.8, -7.53) * mm});
            skLineSegment(sketch, "E775", {"start": v(-0.8, -7.53) * mm, "end": v(-0.75, -7.54) * mm});
            skLineSegment(sketch, "E776", {"start": v(-0.75, -7.54) * mm, "end": v(-0.7, -7.56) * mm});
            skLineSegment(sketch, "E777", {"start": v(-0.7, -7.56) * mm, "end": v(-0.64, -7.58) * mm});
            skLineSegment(sketch, "E778", {"start": v(-0.64, -7.58) * mm, "end": v(-0.6, -7.6) * mm});
            skLineSegment(sketch, "E779", {"start": v(-0.6, -7.6) * mm, "end": v(-0.55, -7.62) * mm});
            skLineSegment(sketch, "E780", {"start": v(-0.55, -7.62) * mm, "end": v(-0.5, -7.64) * mm});
            skLineSegment(sketch, "E781", {"start": v(-0.5, -7.64) * mm, "end": v(-0.41, -7.7) * mm});
            skLineSegment(sketch, "E782", {"start": v(-0.41, -7.7) * mm, "end": v(-0.33, -7.76) * mm});
            skLineSegment(sketch, "E783", {"start": v(-0.33, -7.76) * mm, "end": v(-0.25, -7.83) * mm});
            skLineSegment(sketch, "E784", {"start": v(-0.25, -7.83) * mm, "end": v(-0.18, -7.9) * mm});
            skLineSegment(sketch, "E785", {"start": v(-0.18, -7.9) * mm, "end": v(-0.12, -7.99) * mm});
            skLineSegment(sketch, "E786", {"start": v(-0.12, -7.99) * mm, "end": v(-0.06, -8.08) * mm});
            skLineSegment(sketch, "E787", {"start": v(-0.06, -8.08) * mm, "end": v(-0.04, -8.12) * mm});
            skLineSegment(sketch, "E788", {"start": v(-0.04, -8.12) * mm, "end": v(-0.02, -8.17) * mm});
            skLineSegment(sketch, "E789", {"start": v(-0.02, -8.17) * mm, "end": v(0, -8.22) * mm});
            skLineSegment(sketch, "E790", {"start": v(0, -8.22) * mm, "end": v(0.02, -8.27) * mm});
            skLineSegment(sketch, "E791", {"start": v(0.02, -8.27) * mm, "end": v(0.03, -8.32) * mm});
            skLineSegment(sketch, "E792", {"start": v(0.03, -8.32) * mm, "end": v(0.04, -8.37) * mm});
            skLineSegment(sketch, "E793", {"start": v(0.04, -8.37) * mm, "end": v(0.05, -8.43) * mm});
            skLineSegment(sketch, "E794", {"start": v(0.05, -8.43) * mm, "end": v(0.06, -8.48) * mm});
            skLineSegment(sketch, "E795", {"start": v(0.06, -8.48) * mm, "end": v(0.06, -8.54) * mm});
            skLineSegment(sketch, "E796", {"start": v(0.06, -8.54) * mm, "end": v(0.07, -8.6) * mm});
            skLineSegment(sketch, "E797", {"start": v(0.07, -8.6) * mm, "end": v(0.06, -8.66) * mm});
            skLineSegment(sketch, "E798", {"start": v(0.06, -8.66) * mm, "end": v(0.06, -8.73) * mm});
            skLineSegment(sketch, "E799", {"start": v(0.06, -8.73) * mm, "end": v(0.05, -8.8) * mm});
            skLineSegment(sketch, "E800", {"start": v(0.05, -8.8) * mm, "end": v(0.03, -8.87) * mm});
            skLineSegment(sketch, "E801", {"start": v(0.03, -8.87) * mm, "end": v(0, -8.94) * mm});
            skLineSegment(sketch, "E802", {"start": v(0, -8.94) * mm, "end": v(-0.02, -9) * mm});
            skLineSegment(sketch, "E803", {"start": v(-0.02, -9) * mm, "end": v(-0.04, -9.07) * mm});
            skLineSegment(sketch, "E804", {"start": v(-0.04, -9.07) * mm, "end": v(-0.08, -9.13) * mm});
            skLineSegment(sketch, "E805", {"start": v(-0.08, -9.13) * mm, "end": v(-0.05, -9.12) * mm});
            skLineSegment(sketch, "E806", {"start": v(-0.05, -9.12) * mm, "end": v(-0.02, -9.11) * mm});
            skLineSegment(sketch, "E807", {"start": v(-0.02, -9.11) * mm, "end": v(0.08, -9.08) * mm});
            skLineSegment(sketch, "E808", {"start": v(0.08, -9.08) * mm, "end": v(0.2, -9.03) * mm});
            skLineSegment(sketch, "E809", {"start": v(0.2, -9.03) * mm, "end": v(0.33, -8.97) * mm});
            skLineSegment(sketch, "E810", {"start": v(0.33, -8.97) * mm, "end": v(0.38, -8.94) * mm});
            skLineSegment(sketch, "E811", {"start": v(0.38, -8.94) * mm, "end": v(0.43, -8.9) * mm});
            skLineSegment(sketch, "E812", {"start": v(0.43, -8.9) * mm, "end": v(0.47, -8.87) * mm});
            skLineSegment(sketch, "E813", {"start": v(0.47, -8.87) * mm, "end": v(0.51, -8.83) * mm});
            skLineSegment(sketch, "E814", {"start": v(0.51, -8.83) * mm, "end": v(0.55, -8.78) * mm});
            skLineSegment(sketch, "E815", {"start": v(0.55, -8.78) * mm, "end": v(0.58, -8.74) * mm});
            skLineSegment(sketch, "E816", {"start": v(0.58, -8.74) * mm, "end": v(0.61, -8.69) * mm});
            skLineSegment(sketch, "E817", {"start": v(0.61, -8.69) * mm, "end": v(0.64, -8.64) * mm});
            skLineSegment(sketch, "E818", {"start": v(0.64, -8.64) * mm, "end": v(0.66, -8.58) * mm});
            skLineSegment(sketch, "E819", {"start": v(0.66, -8.58) * mm, "end": v(0.68, -8.53) * mm});
            skLineSegment(sketch, "E820", {"start": v(0.68, -8.53) * mm, "end": v(0.7, -8.47) * mm});
            skLineSegment(sketch, "E821", {"start": v(0.7, -8.47) * mm, "end": v(0.71, -8.4) * mm});
            skLineSegment(sketch, "E822", {"start": v(0.71, -8.4) * mm, "end": v(0.72, -8.34) * mm});
            skLineSegment(sketch, "E823", {"start": v(0.72, -8.34) * mm, "end": v(0.73, -8.28) * mm});
            skLineSegment(sketch, "E824", {"start": v(0.73, -8.28) * mm, "end": v(0.73, -8.21) * mm});
            skLineSegment(sketch, "E825", {"start": v(0.73, -8.21) * mm, "end": v(0.73, -8.15) * mm});
            skLineSegment(sketch, "E826", {"start": v(0.73, -8.15) * mm, "end": v(0.73, -8.08) * mm});
            skLineSegment(sketch, "E827", {"start": v(0.73, -8.08) * mm, "end": v(0.72, -8) * mm});
            skLineSegment(sketch, "E828", {"start": v(0.72, -8) * mm, "end": v(0.7, -7.94) * mm});
            skLineSegment(sketch, "E829", {"start": v(0.7, -7.94) * mm, "end": v(0.7, -7.86) * mm});
            skLineSegment(sketch, "E830", {"start": v(0.7, -7.86) * mm, "end": v(0.67, -7.79) * mm});
            skLineSegment(sketch, "E831", {"start": v(0.67, -7.79) * mm, "end": v(0.65, -7.72) * mm});
            skLineSegment(sketch, "E832", {"start": v(0.65, -7.72) * mm, "end": v(0.63, -7.64) * mm});
            skLineSegment(sketch, "E833", {"start": v(0.63, -7.64) * mm, "end": v(0.6, -7.57) * mm});
            skLineSegment(sketch, "E834", {"start": v(0.6, -7.57) * mm, "end": v(0.57, -7.5) * mm});
            skLineSegment(sketch, "E835", {"start": v(0.57, -7.5) * mm, "end": v(0.53, -7.42) * mm});
            skLineSegment(sketch, "E836", {"start": v(0.53, -7.42) * mm, "end": v(0.5, -7.35) * mm});
            skLineSegment(sketch, "E837", {"start": v(0.5, -7.35) * mm, "end": v(0.45, -7.27) * mm});
            skLineSegment(sketch, "E838", {"start": v(0.45, -7.27) * mm, "end": v(0.4, -7.2) * mm});
            skLineSegment(sketch, "E839", {"start": v(0.4, -7.2) * mm, "end": v(0.35, -7.13) * mm});
            skLineSegment(sketch, "E840", {"start": v(0.35, -7.13) * mm, "end": v(0.3, -7.05) * mm});
            skLineSegment(sketch, "E841", {"start": v(0.3, -7.05) * mm, "end": v(0.25, -6.98) * mm});
            skLineSegment(sketch, "E842", {"start": v(0.25, -6.98) * mm, "end": v(0.12, -6.83) * mm});
            skLineSegment(sketch, "E843", {"start": v(0.12, -6.83) * mm, "end": v(0, -6.7) * mm});
            skLineSegment(sketch, "E844", {"start": v(0, -6.7) * mm, "end": v(-0.12, -6.58) * mm});
            skLineSegment(sketch, "E845", {"start": v(-0.12, -6.58) * mm, "end": v(-0.18, -6.53) * mm});
            skLineSegment(sketch, "E846", {"start": v(-0.18, -6.53) * mm, "end": v(-0.24, -6.48) * mm});
            skLineSegment(sketch, "E847", {"start": v(-0.24, -6.48) * mm, "end": v(-0.3, -6.44) * mm});
            skLineSegment(sketch, "E848", {"start": v(-0.3, -6.44) * mm, "end": v(-0.35, -6.4) * mm});
            skLineSegment(sketch, "E849", {"start": v(-0.35, -6.4) * mm, "end": v(-0.4, -6.37) * mm});
            skLineSegment(sketch, "E850", {"start": v(-0.4, -6.37) * mm, "end": v(-0.46, -6.33) * mm});
            skLineSegment(sketch, "E851", {"start": v(-0.46, -6.33) * mm, "end": v(-0.52, -6.3) * mm});
            skLineSegment(sketch, "E852", {"start": v(-0.52, -6.3) * mm, "end": v(-0.57, -6.28) * mm});
            skLineSegment(sketch, "E853", {"start": v(-0.57, -6.28) * mm, "end": v(-0.63, -6.26) * mm});
            skLineSegment(sketch, "E854", {"start": v(-0.63, -6.26) * mm, "end": v(-0.68, -6.25) * mm});
            skLineSegment(sketch, "E855", {"start": v(-0.68, -6.25) * mm, "end": v(-0.74, -6.24) * mm});
            skLineSegment(sketch, "E856", {"start": v(-0.74, -6.24) * mm, "end": v(-0.8, -6.23) * mm});
            skLineSegment(sketch, "E857", {"start": v(-0.8, -6.23) * mm, "end": v(-0.85, -6.22) * mm});
            skLineSegment(sketch, "E858", {"start": v(-0.85, -6.22) * mm, "end": v(-0.9, -6.22) * mm});
            skLineSegment(sketch, "E859", {"start": v(-0.9, -6.22) * mm, "end": v(-0.96, -6.23) * mm});
            skLineSegment(sketch, "E860", {"start": v(-0.96, -6.23) * mm, "end": v(-1.01, -6.23) * mm});
            skLineSegment(sketch, "E861", {"start": v(-1.01, -6.23) * mm, "end": v(-1.07, -6.25) * mm});
            skLineSegment(sketch, "E862", {"start": v(-1.07, -6.25) * mm, "end": v(-1.13, -6.26) * mm});
            skLineSegment(sketch, "E863", {"start": v(-1.13, -6.26) * mm, "end": v(-1.19, -6.28) * mm});
            skLineSegment(sketch, "E864", {"start": v(-1.19, -6.28) * mm, "end": v(-1.25, -6.3) * mm});
            skLineSegment(sketch, "E865", {"start": v(-1.25, -6.3) * mm, "end": v(-1.3, -6.33) * mm});
            skLineSegment(sketch, "E866", {"start": v(-1.3, -6.33) * mm, "end": v(-1.37, -6.36) * mm});
            skLineSegment(sketch, "E867", {"start": v(-1.37, -6.36) * mm, "end": v(-1.43, -6.4) * mm});
            skLineSegment(sketch, "E868", {"start": v(-1.43, -6.4) * mm, "end": v(-1.5, -6.43) * mm});
            skLineSegment(sketch, "E869", {"start": v(-1.5, -6.43) * mm, "end": v(-1.63, -6.51) * mm});
            skLineSegment(sketch, "E870", {"start": v(-1.63, -6.51) * mm, "end": v(-1.73, -6.58) * mm});
            skLineSegment(sketch, "E871", {"start": v(-1.73, -6.58) * mm, "end": v(-1.83, -6.64) * mm});
            skLineSegment(sketch, "E872", {"start": v(-1.83, -6.64) * mm, "end": v(-1.92, -6.7) * mm});
            skLineSegment(sketch, "E873", {"start": v(-1.92, -6.7) * mm, "end": v(-2.01, -6.74) * mm});
            skLineSegment(sketch, "E874", {"start": v(-2.01, -6.74) * mm, "end": v(-2.1, -6.78) * mm});
            skLineSegment(sketch, "E875", {"start": v(-2.1, -6.78) * mm, "end": v(-2.19, -6.82) * mm});
            skLineSegment(sketch, "E876", {"start": v(-2.19, -6.82) * mm, "end": v(-2.27, -6.84) * mm});
            skLineSegment(sketch, "E877", {"start": v(-2.27, -6.84) * mm, "end": v(-2.34, -6.87) * mm});
            skLineSegment(sketch, "E878", {"start": v(-2.34, -6.87) * mm, "end": v(-2.42, -6.88) * mm});
            skLineSegment(sketch, "E879", {"start": v(-2.42, -6.88) * mm, "end": v(-2.48, -6.9) * mm});
            skLineSegment(sketch, "E880", {"start": v(-2.48, -6.9) * mm, "end": v(-2.54, -6.9) * mm});
            skLineSegment(sketch, "E881", {"start": v(-2.54, -6.9) * mm, "end": v(-2.6, -6.9) * mm});
            skLineSegment(sketch, "E882", {"start": v(-2.6, -6.9) * mm, "end": v(-2.65, -6.9) * mm});
            skLineSegment(sketch, "E883", {"start": v(-2.65, -6.9) * mm, "end": v(-2.7, -6.88) * mm});
            skLineSegment(sketch, "E884", {"start": v(-2.7, -6.88) * mm, "end": v(-2.74, -6.87) * mm});
            skLineSegment(sketch, "E885", {"start": v(-2.74, -6.87) * mm, "end": v(-2.78, -6.85) * mm});
            skLineSegment(sketch, "E886", {"start": v(-2.78, -6.85) * mm, "end": v(-2.8, -6.82) * mm});
            skLineSegment(sketch, "E887", {"start": v(-2.8, -6.82) * mm, "end": v(-2.83, -6.8) * mm});
            skLineSegment(sketch, "E888", {"start": v(-2.83, -6.8) * mm, "end": v(-2.84, -6.76) * mm});
            skLineSegment(sketch, "E889", {"start": v(-2.84, -6.76) * mm, "end": v(-2.85, -6.73) * mm});
            skLineSegment(sketch, "E890", {"start": v(-2.85, -6.73) * mm, "end": v(-2.85, -6.69) * mm});
            skLineSegment(sketch, "E891", {"start": v(-2.85, -6.69) * mm, "end": v(-2.85, -6.64) * mm});
            skLineSegment(sketch, "E892", {"start": v(-2.85, -6.64) * mm, "end": v(-2.83, -6.6) * mm});
            skLineSegment(sketch, "E893", {"start": v(-2.83, -6.6) * mm, "end": v(-2.81, -6.54) * mm});
            skLineSegment(sketch, "E894", {"start": v(-2.81, -6.54) * mm, "end": v(-2.78, -6.49) * mm});
            skLineSegment(sketch, "E895", {"start": v(-2.78, -6.49) * mm, "end": v(-2.74, -6.43) * mm});
            skLineSegment(sketch, "E896", {"start": v(-2.74, -6.43) * mm, "end": v(-2.7, -6.37) * mm});
            skLineSegment(sketch, "E897", {"start": v(-2.7, -6.37) * mm, "end": v(-2.64, -6.3) * mm});
            skLineSegment(sketch, "E898", {"start": v(-2.64, -6.3) * mm, "end": v(-2.58, -6.24) * mm});
            skLineSegment(sketch, "E899", {"start": v(-2.58, -6.24) * mm, "end": v(-2.5, -6.17) * mm});
            skLineSegment(sketch, "E900", {"start": v(-2.5, -6.17) * mm, "end": v(-2.42, -6.1) * mm});
            skLineSegment(sketch, "E901", {"start": v(-2.42, -6.1) * mm, "end": v(-2.33, -6.02) * mm});
            skLineSegment(sketch, "E902", {"start": v(-2.33, -6.02) * mm, "end": v(-2.16, -5.89) * mm});
            skLineSegment(sketch, "E903", {"start": v(-2.16, -5.89) * mm, "end": v(-2.1, -5.83) * mm});
            skLineSegment(sketch, "E904", {"start": v(-2.1, -5.83) * mm, "end": v(-2.04, -5.78) * mm});
            skLineSegment(sketch, "E905", {"start": v(-2.04, -5.78) * mm, "end": v(-2, -5.73) * mm});
            skLineSegment(sketch, "E906", {"start": v(-2, -5.73) * mm, "end": v(-1.97, -5.68) * mm});
            skLineSegment(sketch, "E907", {"start": v(-1.97, -5.68) * mm, "end": v(-1.96, -5.66) * mm});
            skLineSegment(sketch, "E908", {"start": v(-1.96, -5.66) * mm, "end": v(-1.95, -5.63) * mm});
            skLineSegment(sketch, "E909", {"start": v(-1.95, -5.63) * mm, "end": v(-1.94, -5.6) * mm});
            skLineSegment(sketch, "E910", {"start": v(-1.94, -5.6) * mm, "end": v(-1.94, -5.58) * mm});
            skLineSegment(sketch, "E911", {"start": v(-1.94, -5.58) * mm, "end": v(-1.94, -5.56) * mm});
            skLineSegment(sketch, "E912", {"start": v(-1.94, -5.56) * mm, "end": v(-1.95, -5.53) * mm});
            skLineSegment(sketch, "E913", {"start": v(-1.95, -5.53) * mm, "end": v(-1.96, -5.47) * mm});
            skLineSegment(sketch, "E914", {"start": v(-1.96, -5.47) * mm, "end": v(-2, -5.4) * mm});
            skLineSegment(sketch, "E915", {"start": v(-2, -5.4) * mm, "end": v(-2.03, -5.33) * mm});
            skLineSegment(sketch, "E916", {"start": v(-2.03, -5.33) * mm, "end": v(-2.09, -5.25) * mm});
            skLineSegment(sketch, "E917", {"start": v(-2.09, -5.25) * mm, "end": v(-2.15, -5.15) * mm});
            skLineSegment(sketch, "E918", {"start": v(-2.15, -5.15) * mm, "end": v(-2.32, -4.92) * mm});
            skLineSegment(sketch, "E919", {"start": v(-2.32, -4.92) * mm, "end": v(-2.38, -4.82) * mm});
            skLineSegment(sketch, "E920", {"start": v(-2.38, -4.82) * mm, "end": v(-2.44, -4.73) * mm});
            skLineSegment(sketch, "E921", {"start": v(-2.44, -4.73) * mm, "end": v(-2.5, -4.63) * mm});
            skLineSegment(sketch, "E922", {"start": v(-2.5, -4.63) * mm, "end": v(-2.55, -4.52) * mm});
            skLineSegment(sketch, "E923", {"start": v(-2.55, -4.52) * mm, "end": v(-2.6, -4.42) * mm});
            skLineSegment(sketch, "E924", {"start": v(-2.6, -4.42) * mm, "end": v(-2.64, -4.3) * mm});
            skLineSegment(sketch, "E925", {"start": v(-2.64, -4.3) * mm, "end": v(-2.68, -4.2) * mm});
            skLineSegment(sketch, "E926", {"start": v(-2.68, -4.2) * mm, "end": v(-2.71, -4.09) * mm});
            skLineSegment(sketch, "E927", {"start": v(-2.71, -4.09) * mm, "end": v(-2.74, -3.97) * mm});
            skLineSegment(sketch, "E928", {"start": v(-2.74, -3.97) * mm, "end": v(-2.77, -3.86) * mm});
            skLineSegment(sketch, "E929", {"start": v(-2.77, -3.86) * mm, "end": v(-2.79, -3.74) * mm});
            skLineSegment(sketch, "E930", {"start": v(-2.79, -3.74) * mm, "end": v(-2.8, -3.63) * mm});
            skLineSegment(sketch, "E931", {"start": v(-2.8, -3.63) * mm, "end": v(-2.82, -3.51) * mm});
            skLineSegment(sketch, "E932", {"start": v(-2.82, -3.51) * mm, "end": v(-2.83, -3.4) * mm});
            skLineSegment(sketch, "E933", {"start": v(-2.83, -3.4) * mm, "end": v(-2.83, -3.28) * mm});
            skLineSegment(sketch, "E934", {"start": v(-2.83, -3.28) * mm, "end": v(-2.83, -3.16) * mm});
            skLineSegment(sketch, "E935", {"start": v(-2.83, -3.16) * mm, "end": v(-2.83, -3.05) * mm});
            skLineSegment(sketch, "E936", {"start": v(-2.83, -3.05) * mm, "end": v(-2.82, -2.93) * mm});
            skLineSegment(sketch, "E937", {"start": v(-2.82, -2.93) * mm, "end": v(-2.8, -2.82) * mm});
            skLineSegment(sketch, "E938", {"start": v(-2.8, -2.82) * mm, "end": v(-2.79, -2.7) * mm});
            skLineSegment(sketch, "E939", {"start": v(-2.79, -2.7) * mm, "end": v(-2.77, -2.59) * mm});
            skLineSegment(sketch, "E940", {"start": v(-2.77, -2.59) * mm, "end": v(-2.74, -2.48) * mm});
            skLineSegment(sketch, "E941", {"start": v(-2.74, -2.48) * mm, "end": v(-2.71, -2.37) * mm});
            skLineSegment(sketch, "E942", {"start": v(-2.71, -2.37) * mm, "end": v(-2.68, -2.26) * mm});
            skLineSegment(sketch, "E943", {"start": v(-2.68, -2.26) * mm, "end": v(-2.64, -2.16) * mm});
            skLineSegment(sketch, "E944", {"start": v(-2.64, -2.16) * mm, "end": v(-2.6, -2.05) * mm});
            skLineSegment(sketch, "E945", {"start": v(-2.6, -2.05) * mm, "end": v(-2.55, -1.95) * mm});
            skLineSegment(sketch, "E946", {"start": v(-2.55, -1.95) * mm, "end": v(-2.5, -1.86) * mm});
            skLineSegment(sketch, "E947", {"start": v(-2.5, -1.86) * mm, "end": v(-2.44, -1.76) * mm});
            skLineSegment(sketch, "E948", {"start": v(-2.44, -1.76) * mm, "end": v(-2.38, -1.67) * mm});
            skLineSegment(sketch, "E949", {"start": v(-2.38, -1.67) * mm, "end": v(-2.32, -1.59) * mm});
            skLineSegment(sketch, "E950", {"start": v(-2.32, -1.59) * mm, "end": v(-2.25, -1.5) * mm});
            skLineSegment(sketch, "E951", {"start": v(-2.25, -1.5) * mm, "end": v(-2.12, -1.37) * mm});
            skLineSegment(sketch, "E952", {"start": v(-2.12, -1.37) * mm, "end": v(-2, -1.24) * mm});
            skLineSegment(sketch, "E953", {"start": v(-2, -1.24) * mm, "end": v(-1.86, -1.11) * mm});
            skLineSegment(sketch, "E954", {"start": v(-1.86, -1.11) * mm, "end": v(-1.73, -1) * mm});
            skLineSegment(sketch, "E955", {"start": v(-1.73, -1) * mm, "end": v(-1.59, -0.9) * mm});
            skLineSegment(sketch, "E956", {"start": v(-1.59, -0.9) * mm, "end": v(-1.45, -0.8) * mm});
            skLineSegment(sketch, "E957", {"start": v(-1.45, -0.8) * mm, "end": v(-1.3, -0.7) * mm});
            skLineSegment(sketch, "E958", {"start": v(-1.3, -0.7) * mm, "end": v(-1.16, -0.63) * mm});
            skLineSegment(sketch, "E959", {"start": v(-1.16, -0.63) * mm, "end": v(-1.02, -0.56) * mm});
            skLineSegment(sketch, "E960", {"start": v(-1.02, -0.56) * mm, "end": v(-0.87, -0.5) * mm});
            skLineSegment(sketch, "E961", {"start": v(-0.87, -0.5) * mm, "end": v(-0.85, -0.49) * mm});
            skLineSegment(sketch, "E962", {"start": v(-0.85, -0.49) * mm, "end": v(-0.94, -0.46) * mm});
            skLineSegment(sketch, "E963", {"start": v(-0.94, -0.46) * mm, "end": v(-1.04, -0.4) * mm});
            skLineSegment(sketch, "E964", {"start": v(-1.04, -0.4) * mm, "end": v(-1.23, -0.32) * mm});
            skLineSegment(sketch, "E965", {"start": v(-1.23, -0.32) * mm, "end": v(-1.34, -0.27) * mm});
            skLineSegment(sketch, "E966", {"start": v(-1.34, -0.27) * mm, "end": v(-1.41, -0.24) * mm});
            skLineSegment(sketch, "E967", {"start": v(-1.41, -0.24) * mm, "end": v(-1.48, -0.2) * mm});
            skLineSegment(sketch, "E968", {"start": v(-1.48, -0.2) * mm, "end": v(-1.54, -0.15) * mm});
            skLineSegment(sketch, "E969", {"start": v(-1.54, -0.15) * mm, "end": v(-1.6, -0.1) * mm});
            skLineSegment(sketch, "E970", {"start": v(-1.6, -0.1) * mm, "end": v(-1.66, -0.04) * mm});
            skLineSegment(sketch, "E971", {"start": v(-1.66, -0.04) * mm, "end": v(-1.71, 0.02) * mm});
            skLineSegment(sketch, "E972", {"start": v(-1.71, 0.02) * mm, "end": v(-1.76, 0.08) * mm});
            skLineSegment(sketch, "E973", {"start": v(-1.76, 0.08) * mm, "end": v(-1.8, 0.14) * mm});
            skLineSegment(sketch, "E974", {"start": v(-1.8, 0.14) * mm, "end": v(-1.85, 0.2) * mm});
            skLineSegment(sketch, "E975", {"start": v(-1.85, 0.2) * mm, "end": v(-1.89, 0.28) * mm});
            skLineSegment(sketch, "E976", {"start": v(-1.89, 0.28) * mm, "end": v(-1.92, 0.35) * mm});
            skLineSegment(sketch, "E977", {"start": v(-1.92, 0.35) * mm, "end": v(-1.95, 0.43) * mm});
            skLineSegment(sketch, "E978", {"start": v(-1.95, 0.43) * mm, "end": v(-1.97, 0.5) * mm});
            skLineSegment(sketch, "E979", {"start": v(-1.97, 0.5) * mm, "end": v(-1.99, 0.58) * mm});
            skLineSegment(sketch, "E980", {"start": v(-1.99, 0.58) * mm, "end": v(-2, 0.66) * mm});
            skLineSegment(sketch, "E981", {"start": v(-2, 0.66) * mm, "end": v(-2.01, 0.75) * mm});
            skLineSegment(sketch, "E982", {"start": v(-2.01, 0.75) * mm, "end": v(-2.01, 0.83) * mm});
            skLineSegment(sketch, "E983", {"start": v(-2.01, 0.83) * mm, "end": v(-2.01, 0.9) * mm});
            skLineSegment(sketch, "E984", {"start": v(-2.01, 0.9) * mm, "end": v(-2, 0.96) * mm});
            skLineSegment(sketch, "E985", {"start": v(-2, 0.96) * mm, "end": v(-2, 1.02) * mm});
            skLineSegment(sketch, "E986", {"start": v(-2, 1.02) * mm, "end": v(-1.99, 1.08) * mm});
            skLineSegment(sketch, "E987", {"start": v(-1.99, 1.08) * mm, "end": v(-1.98, 1.14) * mm});
            skLineSegment(sketch, "E988", {"start": v(-1.98, 1.14) * mm, "end": v(-1.96, 1.2) * mm});
            skLineSegment(sketch, "E989", {"start": v(-1.96, 1.2) * mm, "end": v(-1.94, 1.26) * mm});
            skLineSegment(sketch, "E990", {"start": v(-1.94, 1.26) * mm, "end": v(-1.92, 1.31) * mm});
            skLineSegment(sketch, "E991", {"start": v(-1.92, 1.31) * mm, "end": v(-1.9, 1.37) * mm});
            skLineSegment(sketch, "E992", {"start": v(-1.9, 1.37) * mm, "end": v(-1.86, 1.42) * mm});
            skLineSegment(sketch, "E993", {"start": v(-1.86, 1.42) * mm, "end": v(-1.83, 1.47) * mm});
            skLineSegment(sketch, "E994", {"start": v(-1.83, 1.47) * mm, "end": v(-1.8, 1.52) * mm});
            skLineSegment(sketch, "E995", {"start": v(-1.8, 1.52) * mm, "end": v(-1.77, 1.57) * mm});
            skLineSegment(sketch, "E996", {"start": v(-1.77, 1.57) * mm, "end": v(-1.73, 1.62) * mm});
            skLineSegment(sketch, "E997", {"start": v(-1.73, 1.62) * mm, "end": v(-1.7, 1.67) * mm});
            skLineSegment(sketch, "E998", {"start": v(-1.7, 1.67) * mm, "end": v(-1.65, 1.7) * mm});
            skLineSegment(sketch, "E999", {"start": v(-1.65, 1.7) * mm, "end": v(-1.6, 1.75) * mm});
            skLineSegment(sketch, "E1000", {"start": v(-1.6, 1.75) * mm, "end": v(-1.56, 1.79) * mm});
            skLineSegment(sketch, "E1001", {"start": v(-1.56, 1.79) * mm, "end": v(-1.52, 1.83) * mm});
            skLineSegment(sketch, "E1002", {"start": v(-1.52, 1.83) * mm, "end": v(-1.47, 1.86) * mm});
            skLineSegment(sketch, "E1003", {"start": v(-1.47, 1.86) * mm, "end": v(-1.42, 1.9) * mm});
            skLineSegment(sketch, "E1004", {"start": v(-1.42, 1.9) * mm, "end": v(-1.36, 1.92) * mm});
            skLineSegment(sketch, "E1005", {"start": v(-1.36, 1.92) * mm, "end": v(-1.31, 1.95) * mm});
            skLineSegment(sketch, "E1006", {"start": v(-1.31, 1.95) * mm, "end": v(-1.26, 1.97) * mm});
            skLineSegment(sketch, "E1007", {"start": v(-1.26, 1.97) * mm, "end": v(-1.2, 2) * mm});
            skLineSegment(sketch, "E1008", {"start": v(-1.2, 2) * mm, "end": v(-1.14, 2.02) * mm});
            skLineSegment(sketch, "E1009", {"start": v(-1.14, 2.02) * mm, "end": v(-1.08, 2.03) * mm});
            skLineSegment(sketch, "E1010", {"start": v(-1.08, 2.03) * mm, "end": v(-1.02, 2.05) * mm});
            skLineSegment(sketch, "E1011", {"start": v(-1.02, 2.05) * mm, "end": v(-0.96, 2.06) * mm});
            skLineSegment(sketch, "E1012", {"start": v(-0.96, 2.06) * mm, "end": v(-0.9, 2.07) * mm});
            skLineSegment(sketch, "E1013", {"start": v(-0.9, 2.07) * mm, "end": v(-0.84, 2.07) * mm});
            skLineSegment(sketch, "E1014", {"start": v(-0.84, 2.07) * mm, "end": v(-0.77, 2.07) * mm});
            skLineSegment(sketch, "E1015", {"start": v(-0.77, 2.07) * mm, "end": v(-0.7, 2.07) * mm});
            skLineSegment(sketch, "E1016", {"start": v(-0.7, 2.07) * mm, "end": v(-0.65, 2.07) * mm});
            skLineSegment(sketch, "E1017", {"start": v(-0.65, 2.07) * mm, "end": v(-0.58, 2.06) * mm});
            skLineSegment(sketch, "E1018", {"start": v(-0.58, 2.06) * mm, "end": v(-0.52, 2.05) * mm});
            skLineSegment(sketch, "E1019", {"start": v(-0.52, 2.05) * mm, "end": v(-0.46, 2.03) * mm});
            skLineSegment(sketch, "E1020", {"start": v(-0.46, 2.03) * mm, "end": v(-0.4, 2.02) * mm});
            skLineSegment(sketch, "E1021", {"start": v(-0.4, 2.02) * mm, "end": v(-0.35, 2) * mm});
            skLineSegment(sketch, "E1022", {"start": v(-0.35, 2) * mm, "end": v(-0.29, 1.97) * mm});
            skLineSegment(sketch, "E1023", {"start": v(-0.29, 1.97) * mm, "end": v(-0.23, 1.95) * mm});
            skLineSegment(sketch, "E1024", {"start": v(-0.23, 1.95) * mm, "end": v(-0.18, 1.92) * mm});
            skLineSegment(sketch, "E1025", {"start": v(-0.18, 1.92) * mm, "end": v(-0.13, 1.9) * mm});
            skLineSegment(sketch, "E1026", {"start": v(-0.13, 1.9) * mm, "end": v(-0.08, 1.86) * mm});
            skLineSegment(sketch, "E1027", {"start": v(-0.08, 1.86) * mm, "end": v(-0.03, 1.83) * mm});
            skLineSegment(sketch, "E1028", {"start": v(-0.03, 1.83) * mm, "end": v(0.02, 1.79) * mm});
            skLineSegment(sketch, "E1029", {"start": v(0.02, 1.79) * mm, "end": v(0.06, 1.75) * mm});
            skLineSegment(sketch, "E1030", {"start": v(0.06, 1.75) * mm, "end": v(0.1, 1.7) * mm});
            skLineSegment(sketch, "E1031", {"start": v(0.1, 1.7) * mm, "end": v(0.15, 1.67) * mm});
            skLineSegment(sketch, "E1032", {"start": v(0.15, 1.67) * mm, "end": v(0.19, 1.62) * mm});
            skLineSegment(sketch, "E1033", {"start": v(0.19, 1.62) * mm, "end": v(0.22, 1.57) * mm});
            skLineSegment(sketch, "E1034", {"start": v(0.22, 1.57) * mm, "end": v(0.26, 1.52) * mm});
            skLineSegment(sketch, "E1035", {"start": v(0.26, 1.52) * mm, "end": v(0.29, 1.47) * mm});
            skLineSegment(sketch, "E1036", {"start": v(0.29, 1.47) * mm, "end": v(0.32, 1.42) * mm});
            skLineSegment(sketch, "E1037", {"start": v(0.32, 1.42) * mm, "end": v(0.35, 1.37) * mm});
            skLineSegment(sketch, "E1038", {"start": v(0.35, 1.37) * mm, "end": v(0.37, 1.31) * mm});
            skLineSegment(sketch, "E1039", {"start": v(0.37, 1.31) * mm, "end": v(0.4, 1.26) * mm});
            skLineSegment(sketch, "E1040", {"start": v(0.4, 1.26) * mm, "end": v(0.41, 1.2) * mm});
            skLineSegment(sketch, "E1041", {"start": v(0.41, 1.2) * mm, "end": v(0.43, 1.14) * mm});
            skLineSegment(sketch, "E1042", {"start": v(0.43, 1.14) * mm, "end": v(0.44, 1.08) * mm});
            skLineSegment(sketch, "E1043", {"start": v(0.44, 1.08) * mm, "end": v(0.45, 1.02) * mm});
            skLineSegment(sketch, "E1044", {"start": v(0.45, 1.02) * mm, "end": v(0.46, 0.96) * mm});
            skLineSegment(sketch, "E1045", {"start": v(0.46, 0.96) * mm, "end": v(0.47, 0.9) * mm});
            skLineSegment(sketch, "E1046", {"start": v(0.47, 0.9) * mm, "end": v(0.47, 0.83) * mm});
            skLineSegment(sketch, "E1047", {"start": v(0.47, 0.83) * mm, "end": v(0.47, 0.77) * mm});
            skLineSegment(sketch, "E1048", {"start": v(0.47, 0.77) * mm, "end": v(0.46, 0.7) * mm});
            skLineSegment(sketch, "E1049", {"start": v(0.46, 0.7) * mm, "end": v(0.46, 0.65) * mm});
            skLineSegment(sketch, "E1050", {"start": v(0.46, 0.65) * mm, "end": v(0.45, 0.6) * mm});
            skLineSegment(sketch, "E1051", {"start": v(0.45, 0.6) * mm, "end": v(0.51, 0.6) * mm});
            skLineSegment(sketch, "E1052", {"start": v(0.51, 0.6) * mm, "end": v(0.59, 0.6) * mm});
            skLineSegment(sketch, "E1053", {"start": v(0.59, 0.6) * mm, "end": v(0.67, 0.62) * mm});
            skLineSegment(sketch, "E1054", {"start": v(0.67, 0.62) * mm, "end": v(0.76, 0.64) * mm});
            skLineSegment(sketch, "E1055", {"start": v(0.76, 0.64) * mm, "end": v(0.88, 0.67) * mm});
            skLineSegment(sketch, "E1056", {"start": v(0.88, 0.67) * mm, "end": v(1, 0.7) * mm});
            skLineSegment(sketch, "E1057", {"start": v(1, 0.7) * mm, "end": v(1.1, 0.75) * mm});
            skLineSegment(sketch, "E1058", {"start": v(1.1, 0.75) * mm, "end": v(1.2, 0.8) * mm});
            skLineSegment(sketch, "E1059", {"start": v(1.2, 0.8) * mm, "end": v(1.3, 0.86) * mm});
            skLineSegment(sketch, "E1060", {"start": v(1.3, 0.86) * mm, "end": v(1.39, 0.92) * mm});
            skLineSegment(sketch, "E1061", {"start": v(1.39, 0.92) * mm, "end": v(1.47, 0.99) * mm});
            skLineSegment(sketch, "E1062", {"start": v(1.47, 0.99) * mm, "end": v(1.55, 1.06) * mm});
            skLineSegment(sketch, "E1063", {"start": v(1.55, 1.06) * mm, "end": v(1.63, 1.14) * mm});
            skLineSegment(sketch, "E1064", {"start": v(1.63, 1.14) * mm, "end": v(1.7, 1.22) * mm});
            skLineSegment(sketch, "E1065", {"start": v(1.7, 1.22) * mm, "end": v(1.76, 1.31) * mm});
            skLineSegment(sketch, "E1066", {"start": v(1.76, 1.31) * mm, "end": v(1.82, 1.4) * mm});
            skLineSegment(sketch, "E1067", {"start": v(1.82, 1.4) * mm, "end": v(1.87, 1.5) * mm});
            skLineSegment(sketch, "E1068", {"start": v(1.87, 1.5) * mm, "end": v(1.91, 1.6) * mm});
            skLineSegment(sketch, "E1069", {"start": v(1.91, 1.6) * mm, "end": v(1.95, 1.7) * mm});
            skLineSegment(sketch, "E1070", {"start": v(1.95, 1.7) * mm, "end": v(1.99, 1.8) * mm});
            skLineSegment(sketch, "E1071", {"start": v(1.99, 1.8) * mm, "end": v(2.01, 1.9) * mm});
            skLineSegment(sketch, "E1072", {"start": v(2.01, 1.9) * mm, "end": v(2.03, 2) * mm});
            skLineSegment(sketch, "E1073", {"start": v(2.03, 2) * mm, "end": v(2.05, 2.12) * mm});
            skLineSegment(sketch, "E1074", {"start": v(2.05, 2.12) * mm, "end": v(2.05, 2.22) * mm});
            skLineSegment(sketch, "E1075", {"start": v(2.05, 2.22) * mm, "end": v(2.05, 2.33) * mm});
            skLineSegment(sketch, "E1076", {"start": v(2.05, 2.33) * mm, "end": v(2.05, 2.44) * mm});
            skLineSegment(sketch, "E1077", {"start": v(2.05, 2.44) * mm, "end": v(2.03, 2.55) * mm});
            skLineSegment(sketch, "E1078", {"start": v(2.03, 2.55) * mm, "end": v(2, 2.66) * mm});
            skLineSegment(sketch, "E1079", {"start": v(2, 2.66) * mm, "end": v(1.98, 2.77) * mm});
            skLineSegment(sketch, "E1080", {"start": v(1.98, 2.77) * mm, "end": v(1.95, 2.87) * mm});
            skLineSegment(sketch, "E1081", {"start": v(1.95, 2.87) * mm, "end": v(1.9, 2.98) * mm});
            skLineSegment(sketch, "E1082", {"start": v(1.9, 2.98) * mm, "end": v(1.85, 3.08) * mm});
            skLineSegment(sketch, "E1083", {"start": v(1.85, 3.08) * mm, "end": v(1.8, 3.18) * mm});
            skLineSegment(sketch, "E1084", {"start": v(1.8, 3.18) * mm, "end": v(1.73, 3.27) * mm});
            skLineSegment(sketch, "E1085", {"start": v(1.73, 3.27) * mm, "end": v(1.65, 3.37) * mm});
            skLineSegment(sketch, "E1086", {"start": v(1.65, 3.37) * mm, "end": v(1.57, 3.46) * mm});
            skLineSegment(sketch, "E1087", {"start": v(1.57, 3.46) * mm, "end": v(1.52, 3.51) * mm});
            skLineSegment(sketch, "E1088", {"start": v(1.52, 3.51) * mm, "end": v(1.46, 3.57) * mm});
            skLineSegment(sketch, "E1089", {"start": v(1.46, 3.57) * mm, "end": v(1.4, 3.62) * mm});
            skLineSegment(sketch, "E1090", {"start": v(1.4, 3.62) * mm, "end": v(1.34, 3.66) * mm});
            skLineSegment(sketch, "E1091", {"start": v(1.34, 3.66) * mm, "end": v(1.28, 3.7) * mm});
            skLineSegment(sketch, "E1092", {"start": v(1.28, 3.7) * mm, "end": v(1.22, 3.74) * mm});
            skLineSegment(sketch, "E1093", {"start": v(1.22, 3.74) * mm, "end": v(1.15, 3.78) * mm});
            skLineSegment(sketch, "E1094", {"start": v(1.15, 3.78) * mm, "end": v(1.1, 3.81) * mm});
            skLineSegment(sketch, "E1095", {"start": v(1.1, 3.81) * mm, "end": v(1.03, 3.84) * mm});
            skLineSegment(sketch, "E1096", {"start": v(1.03, 3.84) * mm, "end": v(0.97, 3.87) * mm});
            skLineSegment(sketch, "E1097", {"start": v(0.97, 3.87) * mm, "end": v(0.9, 3.9) * mm});
            skLineSegment(sketch, "E1098", {"start": v(0.9, 3.9) * mm, "end": v(0.85, 3.92) * mm});
            skLineSegment(sketch, "E1099", {"start": v(0.85, 3.92) * mm, "end": v(0.79, 3.93) * mm});
            skLineSegment(sketch, "E1100", {"start": v(0.79, 3.93) * mm, "end": v(0.73, 3.95) * mm});
            skLineSegment(sketch, "E1101", {"start": v(0.73, 3.95) * mm, "end": v(0.67, 3.96) * mm});
            skLineSegment(sketch, "E1102", {"start": v(0.67, 3.96) * mm, "end": v(0.61, 3.97) * mm});
            skLineSegment(sketch, "E1103", {"start": v(0.61, 3.97) * mm, "end": v(0.56, 3.97) * mm});
            skLineSegment(sketch, "E1104", {"start": v(0.56, 3.97) * mm, "end": v(0.5, 3.97) * mm});
            skLineSegment(sketch, "E1105", {"start": v(0.5, 3.97) * mm, "end": v(0.45, 3.97) * mm});
            skLineSegment(sketch, "E1106", {"start": v(0.45, 3.97) * mm, "end": v(0.4, 3.96) * mm});
            skLineSegment(sketch, "E1107", {"start": v(0.4, 3.96) * mm, "end": v(0.36, 3.95) * mm});
            skLineSegment(sketch, "E1108", {"start": v(0.36, 3.95) * mm, "end": v(0.31, 3.94) * mm});
            skLineSegment(sketch, "E1109", {"start": v(0.31, 3.94) * mm, "end": v(0.27, 3.92) * mm});
            skLineSegment(sketch, "E1110", {"start": v(0.27, 3.92) * mm, "end": v(0.23, 3.9) * mm});
            skLineSegment(sketch, "E1111", {"start": v(0.23, 3.9) * mm, "end": v(0.2, 3.88) * mm});
            skLineSegment(sketch, "E1112", {"start": v(0.2, 3.88) * mm, "end": v(0.17, 3.85) * mm});
            skLineSegment(sketch, "E1113", {"start": v(0.17, 3.85) * mm, "end": v(0.14, 3.82) * mm});
            skLineSegment(sketch, "E1114", {"start": v(0.14, 3.82) * mm, "end": v(0.11, 3.79) * mm});
            skLineSegment(sketch, "E1115", {"start": v(0.11, 3.79) * mm, "end": v(0.1, 3.75) * mm});
            skLineSegment(sketch, "E1116", {"start": v(0.1, 3.75) * mm, "end": v(0.08, 3.7) * mm});
            skLineSegment(sketch, "E1117", {"start": v(0.08, 3.7) * mm, "end": v(0.07, 3.66) * mm});
            skLineSegment(sketch, "E1118", {"start": v(0.07, 3.66) * mm, "end": v(0.06, 3.62) * mm});
            skLineSegment(sketch, "E1119", {"start": v(0.06, 3.62) * mm, "end": v(0.04, 3.53) * mm});
            skLineSegment(sketch, "E1120", {"start": v(0.04, 3.53) * mm, "end": v(0, 3.44) * mm});
            skLineSegment(sketch, "E1121", {"start": v(0, 3.44) * mm, "end": v(-0.03, 3.36) * mm});
            skLineSegment(sketch, "E1122", {"start": v(-0.03, 3.36) * mm, "end": v(-0.08, 3.28) * mm});
            skLineSegment(sketch, "E1123", {"start": v(-0.08, 3.28) * mm, "end": v(-0.13, 3.21) * mm});
            skLineSegment(sketch, "E1124", {"start": v(-0.13, 3.21) * mm, "end": v(-0.18, 3.14) * mm});
            skLineSegment(sketch, "E1125", {"start": v(-0.18, 3.14) * mm, "end": v(-0.24, 3.08) * mm});
            skLineSegment(sketch, "E1126", {"start": v(-0.24, 3.08) * mm, "end": v(-0.31, 3.02) * mm});
            skLineSegment(sketch, "E1127", {"start": v(-0.31, 3.02) * mm, "end": v(-0.38, 2.97) * mm});
            skLineSegment(sketch, "E1128", {"start": v(-0.38, 2.97) * mm, "end": v(-0.46, 2.92) * mm});
            skLineSegment(sketch, "E1129", {"start": v(-0.46, 2.92) * mm, "end": v(-0.53, 2.88) * mm});
            skLineSegment(sketch, "E1130", {"start": v(-0.53, 2.88) * mm, "end": v(-0.62, 2.85) * mm});
            skLineSegment(sketch, "E1131", {"start": v(-0.62, 2.85) * mm, "end": v(-0.7, 2.82) * mm});
            skLineSegment(sketch, "E1132", {"start": v(-0.7, 2.82) * mm, "end": v(-0.8, 2.8) * mm});
            skLineSegment(sketch, "E1133", {"start": v(-0.8, 2.8) * mm, "end": v(-0.88, 2.8) * mm});
            skLineSegment(sketch, "E1134", {"start": v(-0.88, 2.8) * mm, "end": v(-0.97, 2.79) * mm});
            skLineSegment(sketch, "E1135", {"start": v(-0.97, 2.79) * mm, "end": v(-1.03, 2.79) * mm});
            skLineSegment(sketch, "E1136", {"start": v(-1.03, 2.79) * mm, "end": v(-1.08, 2.8) * mm});
            skLineSegment(sketch, "E1137", {"start": v(-1.08, 2.8) * mm, "end": v(-1.14, 2.8) * mm});
            skLineSegment(sketch, "E1138", {"start": v(-1.14, 2.8) * mm, "end": v(-1.19, 2.8) * mm});
            skLineSegment(sketch, "E1139", {"start": v(-1.19, 2.8) * mm, "end": v(-1.24, 2.82) * mm});
            skLineSegment(sketch, "E1140", {"start": v(-1.24, 2.82) * mm, "end": v(-1.3, 2.83) * mm});
            skLineSegment(sketch, "E1141", {"start": v(-1.3, 2.83) * mm, "end": v(-1.34, 2.85) * mm});
            skLineSegment(sketch, "E1142", {"start": v(-1.34, 2.85) * mm, "end": v(-1.39, 2.87) * mm});
            skLineSegment(sketch, "E1143", {"start": v(-1.39, 2.87) * mm, "end": v(-1.48, 2.92) * mm});
            skLineSegment(sketch, "E1144", {"start": v(-1.48, 2.92) * mm, "end": v(-1.57, 2.97) * mm});
            skLineSegment(sketch, "E1145", {"start": v(-1.57, 2.97) * mm, "end": v(-1.65, 3.03) * mm});
            skLineSegment(sketch, "E1146", {"start": v(-1.65, 3.03) * mm, "end": v(-1.72, 3.1) * mm});
            skLineSegment(sketch, "E1147", {"start": v(-1.72, 3.1) * mm, "end": v(-1.8, 3.17) * mm});
            skLineSegment(sketch, "E1148", {"start": v(-1.8, 3.17) * mm, "end": v(-1.85, 3.25) * mm});
            skLineSegment(sketch, "E1149", {"start": v(-1.85, 3.25) * mm, "end": v(-1.9, 3.34) * mm});
            skLineSegment(sketch, "E1150", {"start": v(-1.9, 3.34) * mm, "end": v(-1.95, 3.43) * mm});
            skLineSegment(sketch, "E1151", {"start": v(-1.95, 3.43) * mm, "end": v(-1.97, 3.48) * mm});
            skLineSegment(sketch, "E1152", {"start": v(-1.97, 3.48) * mm, "end": v(-1.99, 3.53) * mm});
            skLineSegment(sketch, "E1153", {"start": v(-1.99, 3.53) * mm, "end": v(-2, 3.58) * mm});
            skLineSegment(sketch, "E1154", {"start": v(-2, 3.58) * mm, "end": v(-2.01, 3.63) * mm});
            skLineSegment(sketch, "E1155", {"start": v(-2.01, 3.63) * mm, "end": v(-2.02, 3.69) * mm});
            skLineSegment(sketch, "E1156", {"start": v(-2.02, 3.69) * mm, "end": v(-2.03, 3.74) * mm});
            skLineSegment(sketch, "E1157", {"start": v(-2.03, 3.74) * mm, "end": v(-2.03, 3.8) * mm});
            skLineSegment(sketch, "E1158", {"start": v(-2.03, 3.8) * mm, "end": v(-2.03, 3.85) * mm});
            skLineSegment(sketch, "E1159", {"start": v(-2.03, 3.85) * mm, "end": v(-2.03, 3.9) * mm});
            skLineSegment(sketch, "E1160", {"start": v(-2.03, 3.9) * mm, "end": v(-2.03, 3.96) * mm});
            skLineSegment(sketch, "E1161", {"start": v(-2.03, 3.96) * mm, "end": v(-2.02, 4.01) * mm});
            skLineSegment(sketch, "E1162", {"start": v(-2.02, 4.01) * mm, "end": v(-2.01, 4.06) * mm});
            skLineSegment(sketch, "E1163", {"start": v(-2.01, 4.06) * mm, "end": v(-2, 4.11) * mm});
            skLineSegment(sketch, "E1164", {"start": v(-2, 4.11) * mm, "end": v(-1.99, 4.17) * mm});
            skLineSegment(sketch, "E1165", {"start": v(-1.99, 4.17) * mm, "end": v(-1.97, 4.22) * mm});
            skLineSegment(sketch, "E1166", {"start": v(-1.97, 4.22) * mm, "end": v(-1.95, 4.26) * mm});
            skLineSegment(sketch, "E1167", {"start": v(-1.95, 4.26) * mm, "end": v(-1.93, 4.31) * mm});
            skLineSegment(sketch, "E1168", {"start": v(-1.93, 4.31) * mm, "end": v(-1.9, 4.36) * mm});
            skLineSegment(sketch, "E1169", {"start": v(-1.9, 4.36) * mm, "end": v(-1.85, 4.45) * mm});
            skLineSegment(sketch, "E1170", {"start": v(-1.85, 4.45) * mm, "end": v(-1.79, 4.53) * mm});
            skLineSegment(sketch, "E1171", {"start": v(-1.79, 4.53) * mm, "end": v(-1.72, 4.6) * mm});
            skLineSegment(sketch, "E1172", {"start": v(-1.72, 4.6) * mm, "end": v(-1.71, 4.61) * mm});
            skLineSegment(sketch, "E1173", {"start": v(-1.71, 4.61) * mm, "end": v(-1.61, 4.74) * mm});
            skLineSegment(sketch, "E1174", {"start": v(-1.61, 4.74) * mm, "end": v(-1.56, 4.81) * mm});
            skLineSegment(sketch, "E1175", {"start": v(-1.56, 4.81) * mm, "end": v(-1.5, 4.88) * mm});
            skLineSegment(sketch, "E1176", {"start": v(-1.5, 4.88) * mm, "end": v(-1.37, 5.05) * mm});
            skLineSegment(sketch, "E1177", {"start": v(-1.37, 5.05) * mm, "end": v(-1.32, 5.12) * mm});
            skLineSegment(sketch, "E1178", {"start": v(-1.32, 5.12) * mm, "end": v(-1.28, 5.19) * mm});
            skLineSegment(sketch, "E1179", {"start": v(-1.28, 5.19) * mm, "end": v(-1.24, 5.25) * mm});
            skLineSegment(sketch, "E1180", {"start": v(-1.24, 5.25) * mm, "end": v(-1.21, 5.3) * mm});
            skLineSegment(sketch, "E1181", {"start": v(-1.21, 5.3) * mm, "end": v(-1.2, 5.35) * mm});
            skLineSegment(sketch, "E1182", {"start": v(-1.2, 5.35) * mm, "end": v(-1.19, 5.4) * mm});
            skLineSegment(sketch, "E1183", {"start": v(-1.19, 5.4) * mm, "end": v(-1.19, 5.44) * mm});
            skLineSegment(sketch, "E1184", {"start": v(-1.19, 5.44) * mm, "end": v(-1.2, 5.48) * mm});
            skLineSegment(sketch, "E1185", {"start": v(-1.2, 5.48) * mm, "end": v(-1.21, 5.53) * mm});
            skLineSegment(sketch, "E1186", {"start": v(-1.21, 5.53) * mm, "end": v(-1.23, 5.57) * mm});
            skLineSegment(sketch, "E1187", {"start": v(-1.23, 5.57) * mm, "end": v(-1.27, 5.62) * mm});
            skLineSegment(sketch, "E1188", {"start": v(-1.27, 5.62) * mm, "end": v(-1.3, 5.68) * mm});
            skLineSegment(sketch, "E1189", {"start": v(-1.3, 5.68) * mm, "end": v(-1.4, 5.8) * mm});
            skLineSegment(sketch, "E1190", {"start": v(-1.4, 5.8) * mm, "end": v(-1.46, 5.85) * mm});
            skLineSegment(sketch, "E1191", {"start": v(-1.46, 5.85) * mm, "end": v(-1.5, 5.91) * mm});
            skLineSegment(sketch, "E1192", {"start": v(-1.5, 5.91) * mm, "end": v(-1.54, 5.98) * mm});
            skLineSegment(sketch, "E1193", {"start": v(-1.54, 5.98) * mm, "end": v(-1.58, 6.04) * mm});
            skLineSegment(sketch, "E1194", {"start": v(-1.58, 6.04) * mm, "end": v(-1.61, 6.11) * mm});
            skLineSegment(sketch, "E1195", {"start": v(-1.61, 6.11) * mm, "end": v(-1.65, 6.18) * mm});
            skLineSegment(sketch, "E1196", {"start": v(-1.65, 6.18) * mm, "end": v(-1.68, 6.26) * mm});
            skLineSegment(sketch, "E1197", {"start": v(-1.68, 6.26) * mm, "end": v(-1.7, 6.34) * mm});
            skLineSegment(sketch, "E1198", {"start": v(-1.7, 6.34) * mm, "end": v(-1.73, 6.42) * mm});
            skLineSegment(sketch, "E1199", {"start": v(-1.73, 6.42) * mm, "end": v(-1.75, 6.5) * mm});
            skLineSegment(sketch, "E1200", {"start": v(-1.75, 6.5) * mm, "end": v(-1.78, 6.59) * mm});
            skLineSegment(sketch, "E1201", {"start": v(-1.78, 6.59) * mm, "end": v(-1.8, 6.68) * mm});
            skLineSegment(sketch, "E1202", {"start": v(-1.8, 6.68) * mm, "end": v(-1.8, 6.76) * mm});
            skLineSegment(sketch, "E1203", {"start": v(-1.8, 6.76) * mm, "end": v(-1.82, 6.85) * mm});
            skLineSegment(sketch, "E1204", {"start": v(-1.82, 6.85) * mm, "end": v(-1.83, 6.94) * mm});
            skLineSegment(sketch, "E1205", {"start": v(-1.83, 6.94) * mm, "end": v(-1.84, 7.04) * mm});
            skLineSegment(sketch, "E1206", {"start": v(-1.84, 7.04) * mm, "end": v(-1.85, 7.13) * mm});
            skLineSegment(sketch, "E1207", {"start": v(-1.85, 7.13) * mm, "end": v(-1.85, 7.22) * mm});
            skLineSegment(sketch, "E1208", {"start": v(-1.85, 7.22) * mm, "end": v(-1.85, 7.31) * mm});
            skLineSegment(sketch, "E1209", {"start": v(-1.85, 7.31) * mm, "end": v(-1.85, 7.4) * mm});
            skLineSegment(sketch, "E1210", {"start": v(-1.85, 7.4) * mm, "end": v(-1.84, 7.5) * mm});
            skLineSegment(sketch, "E1211", {"start": v(-1.84, 7.5) * mm, "end": v(-1.83, 7.6) * mm});
            skLineSegment(sketch, "E1212", {"start": v(-1.83, 7.6) * mm, "end": v(-1.82, 7.68) * mm});
            skLineSegment(sketch, "E1213", {"start": v(-1.82, 7.68) * mm, "end": v(-1.8, 7.77) * mm});
            skLineSegment(sketch, "E1214", {"start": v(-1.8, 7.77) * mm, "end": v(-1.8, 7.86) * mm});
            skLineSegment(sketch, "E1215", {"start": v(-1.8, 7.86) * mm, "end": v(-1.77, 7.95) * mm});
            skLineSegment(sketch, "E1216", {"start": v(-1.77, 7.95) * mm, "end": v(-1.75, 8.03) * mm});
            skLineSegment(sketch, "E1217", {"start": v(-1.75, 8.03) * mm, "end": v(-1.73, 8.12) * mm});
            skLineSegment(sketch, "E1218", {"start": v(-1.73, 8.12) * mm, "end": v(-1.7, 8.2) * mm});
            skLineSegment(sketch, "E1219", {"start": v(-1.7, 8.2) * mm, "end": v(-1.67, 8.28) * mm});
            skLineSegment(sketch, "E1220", {"start": v(-1.67, 8.28) * mm, "end": v(-1.64, 8.36) * mm});
            skLineSegment(sketch, "E1221", {"start": v(-1.64, 8.36) * mm, "end": v(-1.6, 8.43) * mm});
            skLineSegment(sketch, "E1222", {"start": v(-1.6, 8.43) * mm, "end": v(-1.52, 8.6) * mm});
            skLineSegment(sketch, "E1223", {"start": v(-1.52, 8.6) * mm, "end": v(-1.45, 8.73) * mm});
            skLineSegment(sketch, "E1224", {"start": v(-1.45, 8.73) * mm, "end": v(-1.43, 8.79) * mm});
            skLineSegment(sketch, "E1225", {"start": v(-1.43, 8.79) * mm, "end": v(-1.4, 8.84) * mm});
            skLineSegment(sketch, "E1226", {"start": v(-1.4, 8.84) * mm, "end": v(-1.4, 8.9) * mm});
            skLineSegment(sketch, "E1227", {"start": v(-1.4, 8.9) * mm, "end": v(-1.4, 8.93) * mm});
            skLineSegment(sketch, "E1228", {"start": v(-1.4, 8.93) * mm, "end": v(-1.35, 9.23) * mm});
            skLineSegment(sketch, "E1229", {"start": v(-1.35, 9.23) * mm, "end": v(-1.3, 9.64) * mm});
            skLineSegment(sketch, "E1230", {"start": v(-1.3, 9.64) * mm, "end": v(-1.26, 10.13) * mm});
            skLineSegment(sketch, "E1231", {"start": v(-1.26, 10.13) * mm, "end": v(-1.2, 10.68) * mm});
            skLineSegment(sketch, "E1232", {"start": v(-1.2, 10.68) * mm, "end": v(-1.1, 11.92) * mm});
            skLineSegment(sketch, "E1233", {"start": v(-1.1, 11.92) * mm, "end": v(-1, 13.23) * mm});
            skLineSegment(sketch, "E1234", {"start": v(-1, 13.23) * mm, "end": v(-0.9, 14.52) * mm});
            skLineSegment(sketch, "E1235", {"start": v(-0.9, 14.52) * mm, "end": v(-0.15, 30.03) * mm});
            skLineSegment(sketch, "E1236", {"start": v(1.71, -16.42) * mm, "end": v(1.7, -16.32) * mm});
            skLineSegment(sketch, "E1237", {"start": v(1.7, -16.32) * mm, "end": v(1.7, -16.22) * mm});
            skLineSegment(sketch, "E1238", {"start": v(1.7, -16.22) * mm, "end": v(1.68, -16.12) * mm});
            skLineSegment(sketch, "E1239", {"start": v(1.68, -16.12) * mm, "end": v(1.66, -16.03) * mm});
            skLineSegment(sketch, "E1240", {"start": v(1.66, -16.03) * mm, "end": v(1.63, -15.93) * mm});
            skLineSegment(sketch, "E1241", {"start": v(1.63, -15.93) * mm, "end": v(1.6, -15.84) * mm});
            skLineSegment(sketch, "E1242", {"start": v(1.6, -15.84) * mm, "end": v(1.56, -15.75) * mm});
            skLineSegment(sketch, "E1243", {"start": v(1.56, -15.75) * mm, "end": v(1.52, -15.66) * mm});
            skLineSegment(sketch, "E1244", {"start": v(1.52, -15.66) * mm, "end": v(1.47, -15.57) * mm});
            skLineSegment(sketch, "E1245", {"start": v(1.47, -15.57) * mm, "end": v(1.4, -15.5) * mm});
            skLineSegment(sketch, "E1246", {"start": v(1.4, -15.5) * mm, "end": v(1.35, -15.41) * mm});
            skLineSegment(sketch, "E1247", {"start": v(1.35, -15.41) * mm, "end": v(1.28, -15.34) * mm});
            skLineSegment(sketch, "E1248", {"start": v(1.28, -15.34) * mm, "end": v(1.21, -15.27) * mm});
            skLineSegment(sketch, "E1249", {"start": v(1.21, -15.27) * mm, "end": v(1.14, -15.2) * mm});
            skLineSegment(sketch, "E1250", {"start": v(1.14, -15.2) * mm, "end": v(1.06, -15.14) * mm});
            skLineSegment(sketch, "E1251", {"start": v(1.06, -15.14) * mm, "end": v(0.98, -15.09) * mm});
            skLineSegment(sketch, "E1252", {"start": v(0.98, -15.09) * mm, "end": v(0.9, -15.04) * mm});
            skLineSegment(sketch, "E1253", {"start": v(0.9, -15.04) * mm, "end": v(0.8, -15) * mm});
            skLineSegment(sketch, "E1254", {"start": v(0.8, -15) * mm, "end": v(0.72, -14.95) * mm});
            skLineSegment(sketch, "E1255", {"start": v(0.72, -14.95) * mm, "end": v(0.62, -14.92) * mm});
            skLineSegment(sketch, "E1256", {"start": v(0.62, -14.92) * mm, "end": v(0.53, -14.9) * mm});
            skLineSegment(sketch, "E1257", {"start": v(0.53, -14.9) * mm, "end": v(0.43, -14.87) * mm});
            skLineSegment(sketch, "E1258", {"start": v(0.43, -14.87) * mm, "end": v(0.33, -14.85) * mm});
            skLineSegment(sketch, "E1259", {"start": v(0.33, -14.85) * mm, "end": v(0.23, -14.84) * mm});
            skLineSegment(sketch, "E1260", {"start": v(0.23, -14.84) * mm, "end": v(0.14, -14.84) * mm});
            skLineSegment(sketch, "E1261", {"start": v(0.14, -14.84) * mm, "end": v(0.04, -14.84) * mm});
            skLineSegment(sketch, "E1262", {"start": v(0.04, -14.84) * mm, "end": v(-0.06, -14.85) * mm});
            skLineSegment(sketch, "E1263", {"start": v(-0.06, -14.85) * mm, "end": v(-0.16, -14.87) * mm});
            skLineSegment(sketch, "E1264", {"start": v(-0.16, -14.87) * mm, "end": v(-0.26, -14.89) * mm});
            skLineSegment(sketch, "E1265", {"start": v(-0.26, -14.89) * mm, "end": v(-0.35, -14.92) * mm});
            skLineSegment(sketch, "E1266", {"start": v(-0.35, -14.92) * mm, "end": v(-0.45, -14.95) * mm});
            skLineSegment(sketch, "E1267", {"start": v(-0.45, -14.95) * mm, "end": v(-0.54, -14.99) * mm});
            skLineSegment(sketch, "E1268", {"start": v(-0.54, -14.99) * mm, "end": v(-0.62, -15.03) * mm});
            skLineSegment(sketch, "E1269", {"start": v(-0.62, -15.03) * mm, "end": v(-0.71, -15.08) * mm});
            skLineSegment(sketch, "E1270", {"start": v(-0.71, -15.08) * mm, "end": v(-0.8, -15.14) * mm});
            skLineSegment(sketch, "E1271", {"start": v(-0.8, -15.14) * mm, "end": v(-0.87, -15.2) * mm});
            skLineSegment(sketch, "E1272", {"start": v(-0.87, -15.2) * mm, "end": v(-0.95, -15.26) * mm});
            skLineSegment(sketch, "E1273", {"start": v(-0.95, -15.26) * mm, "end": v(-1.02, -15.33) * mm});
            skLineSegment(sketch, "E1274", {"start": v(-1.02, -15.33) * mm, "end": v(-1.08, -15.4) * mm});
            skLineSegment(sketch, "E1275", {"start": v(-1.08, -15.4) * mm, "end": v(-1.14, -15.49) * mm});
            skLineSegment(sketch, "E1276", {"start": v(-1.14, -15.49) * mm, "end": v(-1.2, -15.57) * mm});
            skLineSegment(sketch, "E1277", {"start": v(-1.2, -15.57) * mm, "end": v(-1.25, -15.65) * mm});
            skLineSegment(sketch, "E1278", {"start": v(-1.25, -15.65) * mm, "end": v(-1.3, -15.74) * mm});
            skLineSegment(sketch, "E1279", {"start": v(-1.3, -15.74) * mm, "end": v(-1.33, -15.83) * mm});
            skLineSegment(sketch, "E1280", {"start": v(-1.33, -15.83) * mm, "end": v(-1.37, -15.93) * mm});
            skLineSegment(sketch, "E1281", {"start": v(-1.37, -15.93) * mm, "end": v(-1.4, -16.02) * mm});
            skLineSegment(sketch, "E1282", {"start": v(-1.4, -16.02) * mm, "end": v(-1.42, -16.12) * mm});
            skLineSegment(sketch, "E1283", {"start": v(-1.42, -16.12) * mm, "end": v(-1.43, -16.21) * mm});
            skLineSegment(sketch, "E1284", {"start": v(-1.43, -16.21) * mm, "end": v(-1.44, -16.31) * mm});
            skLineSegment(sketch, "E1285", {"start": v(-1.44, -16.31) * mm, "end": v(-1.45, -16.41) * mm});
            skLineSegment(sketch, "E1286", {"start": v(-1.45, -16.41) * mm, "end": v(-1.45, -16.51) * mm});
            skLineSegment(sketch, "E1287", {"start": v(-1.45, -16.51) * mm, "end": v(-1.44, -16.6) * mm});
            skLineSegment(sketch, "E1288", {"start": v(-1.44, -16.6) * mm, "end": v(-1.42, -16.7) * mm});
            skLineSegment(sketch, "E1289", {"start": v(-1.42, -16.7) * mm, "end": v(-1.4, -16.8) * mm});
            skLineSegment(sketch, "E1290", {"start": v(-1.4, -16.8) * mm, "end": v(-1.37, -16.9) * mm});
            skLineSegment(sketch, "E1291", {"start": v(-1.37, -16.9) * mm, "end": v(-1.34, -17) * mm});
            skLineSegment(sketch, "E1292", {"start": v(-1.34, -17) * mm, "end": v(-1.3, -17.08) * mm});
            skLineSegment(sketch, "E1293", {"start": v(-1.3, -17.08) * mm, "end": v(-1.26, -17.17) * mm});
            skLineSegment(sketch, "E1294", {"start": v(-1.26, -17.17) * mm, "end": v(-1.2, -17.26) * mm});
            skLineSegment(sketch, "E1295", {"start": v(-1.2, -17.26) * mm, "end": v(-1.15, -17.34) * mm});
            skLineSegment(sketch, "E1296", {"start": v(-1.15, -17.34) * mm, "end": v(-1.1, -17.42) * mm});
            skLineSegment(sketch, "E1297", {"start": v(-1.1, -17.42) * mm, "end": v(-1.03, -17.5) * mm});
            skLineSegment(sketch, "E1298", {"start": v(-1.03, -17.5) * mm, "end": v(-0.96, -17.56) * mm});
            skLineSegment(sketch, "E1299", {"start": v(-0.96, -17.56) * mm, "end": v(-0.88, -17.63) * mm});
            skLineSegment(sketch, "E1300", {"start": v(-0.88, -17.63) * mm, "end": v(-0.8, -17.7) * mm});
            skLineSegment(sketch, "E1301", {"start": v(-0.8, -17.7) * mm, "end": v(-0.72, -17.75) * mm});
            skLineSegment(sketch, "E1302", {"start": v(-0.72, -17.75) * mm, "end": v(-0.64, -17.8) * mm});
            skLineSegment(sketch, "E1303", {"start": v(-0.64, -17.8) * mm, "end": v(-0.55, -17.84) * mm});
            skLineSegment(sketch, "E1304", {"start": v(-0.55, -17.84) * mm, "end": v(-0.46, -17.88) * mm});
            skLineSegment(sketch, "E1305", {"start": v(-0.46, -17.88) * mm, "end": v(-0.37, -17.92) * mm});
            skLineSegment(sketch, "E1306", {"start": v(-0.37, -17.92) * mm, "end": v(-0.27, -17.95) * mm});
            skLineSegment(sketch, "E1307", {"start": v(-0.27, -17.95) * mm, "end": v(-0.18, -17.97) * mm});
            skLineSegment(sketch, "E1308", {"start": v(-0.18, -17.97) * mm, "end": v(-0.08, -17.99) * mm});
            skLineSegment(sketch, "E1309", {"start": v(-0.08, -17.99) * mm, "end": v(0.02, -18) * mm});
            skLineSegment(sketch, "E1310", {"start": v(0.02, -18) * mm, "end": v(0.12, -18) * mm});
            skLineSegment(sketch, "E1311", {"start": v(0.12, -18) * mm, "end": v(0.22, -18) * mm});
            skLineSegment(sketch, "E1312", {"start": v(0.22, -18) * mm, "end": v(0.32, -17.99) * mm});
            skLineSegment(sketch, "E1313", {"start": v(0.32, -17.99) * mm, "end": v(0.42, -17.97) * mm});
            skLineSegment(sketch, "E1314", {"start": v(0.42, -17.97) * mm, "end": v(0.51, -17.95) * mm});
            skLineSegment(sketch, "E1315", {"start": v(0.51, -17.95) * mm, "end": v(0.6, -17.93) * mm});
            skLineSegment(sketch, "E1316", {"start": v(0.6, -17.93) * mm, "end": v(0.7, -17.9) * mm});
            skLineSegment(sketch, "E1317", {"start": v(0.7, -17.9) * mm, "end": v(0.8, -17.85) * mm});
            skLineSegment(sketch, "E1318", {"start": v(0.8, -17.85) * mm, "end": v(0.88, -17.81) * mm});
            skLineSegment(sketch, "E1319", {"start": v(0.88, -17.81) * mm, "end": v(0.97, -17.76) * mm});
            skLineSegment(sketch, "E1320", {"start": v(0.97, -17.76) * mm, "end": v(1.05, -17.7) * mm});
            skLineSegment(sketch, "E1321", {"start": v(1.05, -17.7) * mm, "end": v(1.13, -17.65) * mm});
            skLineSegment(sketch, "E1322", {"start": v(1.13, -17.65) * mm, "end": v(1.2, -17.58) * mm});
            skLineSegment(sketch, "E1323", {"start": v(1.2, -17.58) * mm, "end": v(1.27, -17.51) * mm});
            skLineSegment(sketch, "E1324", {"start": v(1.27, -17.51) * mm, "end": v(1.34, -17.44) * mm});
            skLineSegment(sketch, "E1325", {"start": v(1.34, -17.44) * mm, "end": v(1.4, -17.36) * mm});
            skLineSegment(sketch, "E1326", {"start": v(1.4, -17.36) * mm, "end": v(1.46, -17.28) * mm});
            skLineSegment(sketch, "E1327", {"start": v(1.46, -17.28) * mm, "end": v(1.5, -17.2) * mm});
            skLineSegment(sketch, "E1328", {"start": v(1.5, -17.2) * mm, "end": v(1.55, -17.1) * mm});
            skLineSegment(sketch, "E1329", {"start": v(1.55, -17.1) * mm, "end": v(1.6, -17.02) * mm});
            skLineSegment(sketch, "E1330", {"start": v(1.6, -17.02) * mm, "end": v(1.63, -16.92) * mm});
            skLineSegment(sketch, "E1331", {"start": v(1.63, -16.92) * mm, "end": v(1.66, -16.83) * mm});
            skLineSegment(sketch, "E1332", {"start": v(1.66, -16.83) * mm, "end": v(1.68, -16.73) * mm});
            skLineSegment(sketch, "E1333", {"start": v(1.68, -16.73) * mm, "end": v(1.7, -16.63) * mm});
            skLineSegment(sketch, "E1334", {"start": v(1.7, -16.63) * mm, "end": v(1.7, -16.53) * mm});
            skLineSegment(sketch, "E1335", {"start": v(1.7, -16.53) * mm, "end": v(1.71, -16.42) * mm});
            skLineSegment(sketch, "E1336", {"start": v(-1.45, -16.41) * mm, "end": v(1.71, -16.42) * mm, "construction": true});
            skPoint(sketch, "E1337", {"position": v(0.13, -16.42) * mm});
            skCircle(sketch, "E1338", {"center": v(0.13, -16.42) * mm, "radius": 3 * mm});
            skSolve(sketch);
        }
        {
            var Q0;
            Q0=makeQuery(id+"F0.imprint","IMPRINT",FACE,{"disambiguationData":[TD([[makeQuery(id+"F0.imprint","IMPRINT",EDGE,{"derivedFrom":sQuery(id+"F0.wireOp",EDGE,"E0")}),-1.0]])]});
            var Q1;
            {var subQ5=sQuery(id+"F0.wireOp",EDGE,"E528");Q1=makeQuery(id+"F0.imprint","IMPRINT",FACE,{"disambiguationData":[TD([[makeQuery(id+"F0.imprint","IMPRINT",EDGE,{"derivedFrom":subQ5}),1.0]])]});}
            var Q2;
            {var subQ4=sQuery(id+"F0.wireOp",EDGE,"E528");Q2=makeQuery(id+"F0.imprint","IMPRINT",FACE,{"disambiguationData":[TD([[makeQuery(id+"F0.imprint","IMPRINT",EDGE,{"derivedFrom":subQ4}),-1.0]])]});}
            var Q3;
            {var subQ0=sQuery(id+"F0.wireOp",EDGE,"E672");Q3=makeQuery(id+"F0.imprint","IMPRINT",FACE,{"disambiguationData":[TD([[makeQuery(id+"F0.imprint","IMPRINT",EDGE,{"derivedFrom":subQ0}),1.0]])]});}
            var Q4;
            {var subQ0=sQuery(id+"F0.wireOp",EDGE,"E570");Q4=makeQuery(id+"F0.imprint","IMPRINT",FACE,{"disambiguationData":[TD([[makeQuery(id+"F0.imprint","IMPRINT",EDGE,{"derivedFrom":subQ0}),-1.0]])]});}
            extrude(context, id + "F1", {"entities" : qUnion([Q0, Q1, Q2, Q3, Q4]), "depth" : 3 * mm});
        }
    });
